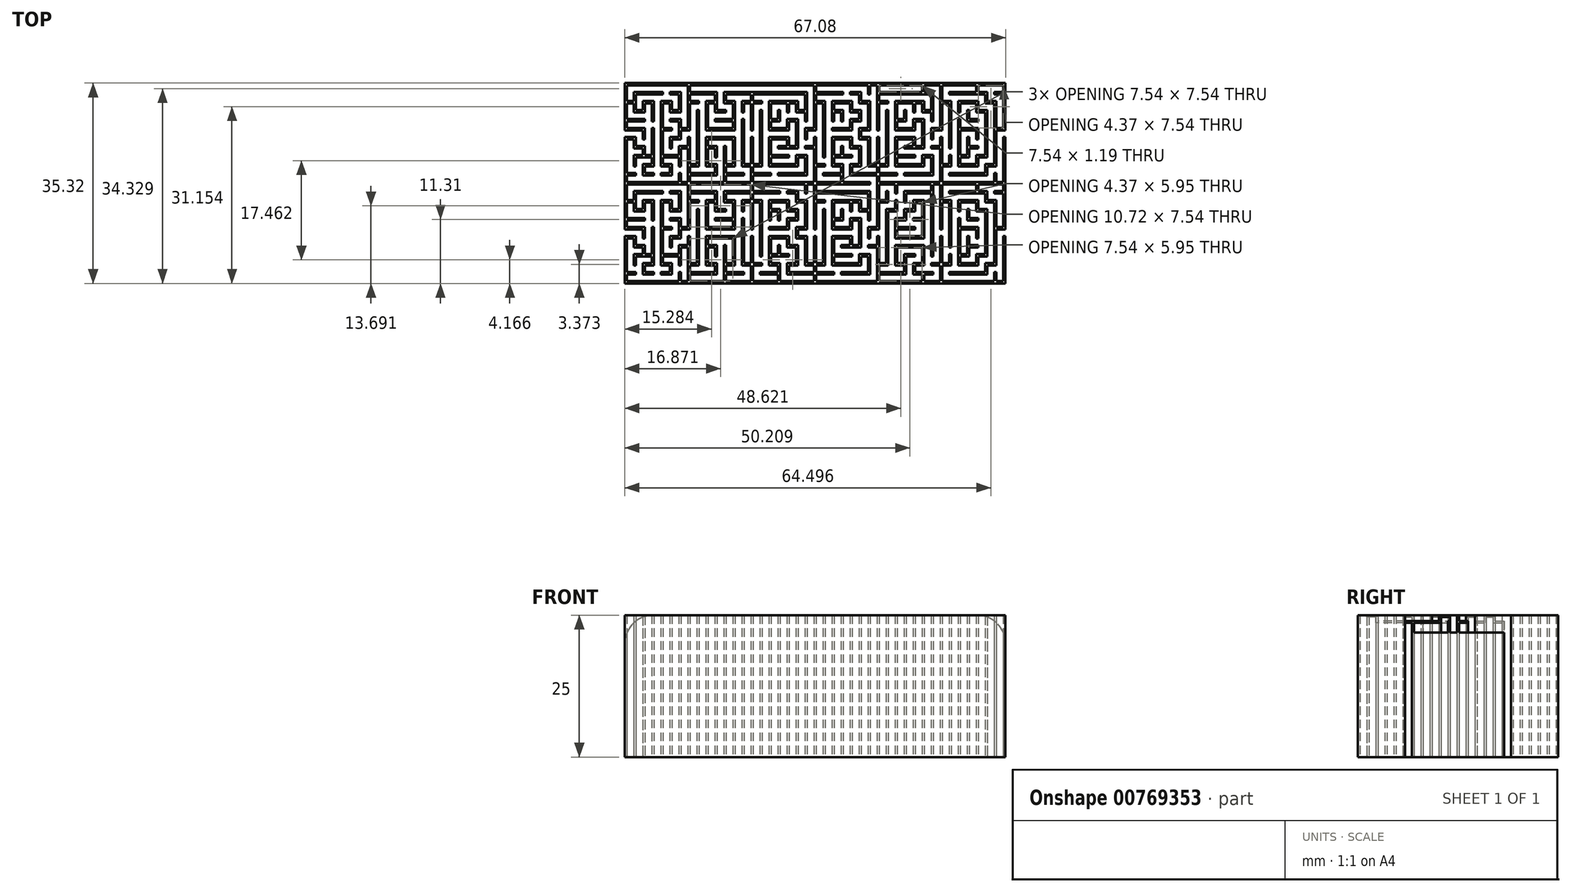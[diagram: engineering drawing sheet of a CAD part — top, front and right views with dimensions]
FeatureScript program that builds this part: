
annotation { "Feature Type Name" : "Feature", "Feature Type Description" : "" }
export const myFeature = defineFeature(function(context is Context, id is Id, definition is map)
    precondition{}
    {
        {
            var Q0;
            Q0=qCreatedBy(makeId("Top.planeOp"),FACE);
            var sketch = newSketch(context, id + "F0", { "sketchPlane" : qUnion([Q0])});
            skLineSegment(sketch, "E0", {"start": v(-25.6, 6.15) * mm, "end": v(-25.6, 8.14) * mm});
            skLineSegment(sketch, "E1", {"start": v(-25.6, 8.14) * mm, "end": v(-24.01, 8.14) * mm});
            skLineSegment(sketch, "E2", {"start": v(-24.01, 8.14) * mm, "end": v(-24.01, 10.91) * mm});
            skLineSegment(sketch, "E3", {"start": v(-24.01, 10.91) * mm, "end": v(-25.6, 10.91) * mm});
            skLineSegment(sketch, "E4", {"start": v(-25.6, 10.91) * mm, "end": v(-25.6, 11.31) * mm});
            skLineSegment(sketch, "E5", {"start": v(-25.6, 11.31) * mm, "end": v(-23.61, 11.31) * mm});
            skLineSegment(sketch, "E6", {"start": v(-23.61, 11.31) * mm, "end": v(-23.61, 9.72) * mm});
            skLineSegment(sketch, "E7", {"start": v(-23.61, 9.72) * mm, "end": v(-22.42, 9.72) * mm});
            skLineSegment(sketch, "E8", {"start": v(-22.42, 9.72) * mm, "end": v(-22.42, 17.26) * mm});
            skLineSegment(sketch, "E9", {"start": v(-22.42, 17.26) * mm, "end": v(-33.14, 17.26) * mm});
            skLineSegment(sketch, "E10", {"start": v(-33.14, 17.26) * mm, "end": v(-33.14, 14.49) * mm});
            skLineSegment(sketch, "E11", {"start": v(-33.14, 14.49) * mm, "end": v(-31.95, 14.49) * mm});
            skLineSegment(sketch, "E12", {"start": v(-31.95, 14.49) * mm, "end": v(-31.95, 16.07) * mm});
            skLineSegment(sketch, "E13", {"start": v(-31.95, 16.07) * mm, "end": v(-26.79, 16.07) * mm});
            skLineSegment(sketch, "E14", {"start": v(-26.79, 16.07) * mm, "end": v(-26.79, 15.68) * mm});
            skLineSegment(sketch, "E15", {"start": v(-26.79, 15.68) * mm, "end": v(-31.55, 15.68) * mm});
            skLineSegment(sketch, "E16", {"start": v(-31.55, 15.68) * mm, "end": v(-31.55, 12.9) * mm});
            skLineSegment(sketch, "E17", {"start": v(-31.55, 12.9) * mm, "end": v(-30.36, 12.9) * mm});
            skLineSegment(sketch, "E18", {"start": v(-30.36, 12.9) * mm, "end": v(-30.36, 14.49) * mm});
            skLineSegment(sketch, "E19", {"start": v(-30.36, 14.49) * mm, "end": v(-28.38, 14.49) * mm});
            skLineSegment(sketch, "E20", {"start": v(-28.38, 14.49) * mm, "end": v(-28.38, 10.91) * mm});
            skLineSegment(sketch, "E21", {"start": v(-28.38, 10.91) * mm, "end": v(-28.77, 10.91) * mm});
            skLineSegment(sketch, "E22", {"start": v(-28.77, 10.91) * mm, "end": v(-28.77, 14.09) * mm});
            skLineSegment(sketch, "E23", {"start": v(-28.77, 14.09) * mm, "end": v(-29.96, 14.09) * mm});
            skLineSegment(sketch, "E24", {"start": v(-29.96, 14.09) * mm, "end": v(-29.96, 12.5) * mm});
            skLineSegment(sketch, "E25", {"start": v(-29.96, 12.5) * mm, "end": v(-31.95, 12.5) * mm});
            skLineSegment(sketch, "E26", {"start": v(-31.95, 12.5) * mm, "end": v(-31.95, 14.09) * mm});
            skLineSegment(sketch, "E27", {"start": v(-31.95, 14.09) * mm, "end": v(-33.14, 14.09) * mm});
            skLineSegment(sketch, "E28", {"start": v(-33.14, 14.09) * mm, "end": v(-33.14, 11.31) * mm});
            skLineSegment(sketch, "E29", {"start": v(-33.14, 11.31) * mm, "end": v(-29.96, 11.31) * mm});
            skLineSegment(sketch, "E30", {"start": v(-29.96, 11.31) * mm, "end": v(-29.96, 10.91) * mm});
            skLineSegment(sketch, "E31", {"start": v(-29.96, 10.91) * mm, "end": v(-33.14, 10.91) * mm});
            skLineSegment(sketch, "E32", {"start": v(-33.14, 10.91) * mm, "end": v(-33.14, 9.72) * mm});
            skLineSegment(sketch, "E33", {"start": v(-33.14, 9.72) * mm, "end": v(-29.96, 9.72) * mm});
            skLineSegment(sketch, "E34", {"start": v(-29.96, 9.72) * mm, "end": v(-29.96, 7.74) * mm});
            skLineSegment(sketch, "E35", {"start": v(-29.96, 7.74) * mm, "end": v(-30.36, 7.74) * mm});
            skLineSegment(sketch, "E36", {"start": v(-30.36, 7.74) * mm, "end": v(-30.36, 9.33) * mm});
            skLineSegment(sketch, "E37", {"start": v(-30.36, 9.33) * mm, "end": v(-33.54, 9.33) * mm});
            skLineSegment(sketch, "E38", {"start": v(-33.54, 9.33) * mm, "end": v(-33.54, 17.66) * mm});
            skLineSegment(sketch, "E39", {"start": v(-33.54, 17.66) * mm, "end": v(-22.03, 17.66) * mm});
            skLineSegment(sketch, "E40", {"start": v(-22.03, 17.66) * mm, "end": v(-22.03, 9.33) * mm});
            skLineSegment(sketch, "E41", {"start": v(-22.03, 9.33) * mm, "end": v(-23.61, 9.33) * mm});
            skLineSegment(sketch, "E42", {"start": v(-23.61, 9.33) * mm, "end": v(-23.61, 7.74) * mm});
            skLineSegment(sketch, "E43", {"start": v(-23.61, 7.74) * mm, "end": v(-25.2, 7.74) * mm});
            skLineSegment(sketch, "E44", {"start": v(-25.2, 7.74) * mm, "end": v(-25.2, 6.15) * mm});
            skLineSegment(sketch, "E45", {"start": v(-25.2, 6.15) * mm, "end": v(-25.6, 6.15) * mm});
            skLineSegment(sketch, "E46", {"start": v(-33.54, -0.2) * mm, "end": v(-33.54, 8.14) * mm});
            skLineSegment(sketch, "E47", {"start": v(-33.54, 8.14) * mm, "end": v(-31.55, 8.14) * mm});
            skLineSegment(sketch, "E48", {"start": v(-31.55, 8.14) * mm, "end": v(-31.55, 6.55) * mm});
            skLineSegment(sketch, "E49", {"start": v(-31.55, 6.55) * mm, "end": v(-29.96, 6.55) * mm});
            skLineSegment(sketch, "E50", {"start": v(-29.96, 6.55) * mm, "end": v(-29.96, 4.96) * mm});
            skLineSegment(sketch, "E51", {"start": v(-29.96, 4.96) * mm, "end": v(-28.77, 4.96) * mm});
            skLineSegment(sketch, "E52", {"start": v(-28.77, 4.96) * mm, "end": v(-28.77, 9.72) * mm});
            skLineSegment(sketch, "E53", {"start": v(-28.77, 9.72) * mm, "end": v(-28.38, 9.72) * mm});
            skLineSegment(sketch, "E54", {"start": v(-28.38, 9.72) * mm, "end": v(-28.38, 2.98) * mm});
            skLineSegment(sketch, "E55", {"start": v(-28.38, 2.98) * mm, "end": v(-29.96, 2.98) * mm});
            skLineSegment(sketch, "E56", {"start": v(-29.96, 2.98) * mm, "end": v(-29.96, 1.79) * mm});
            skLineSegment(sketch, "E57", {"start": v(-29.96, 1.79) * mm, "end": v(-28.38, 1.79) * mm});
            skLineSegment(sketch, "E58", {"start": v(-28.38, 1.79) * mm, "end": v(-28.38, 1.39) * mm});
            skLineSegment(sketch, "E59", {"start": v(-28.38, 1.39) * mm, "end": v(-30.36, 1.39) * mm});
            skLineSegment(sketch, "E60", {"start": v(-30.36, 1.39) * mm, "end": v(-30.36, 3.37) * mm});
            skLineSegment(sketch, "E61", {"start": v(-30.36, 3.37) * mm, "end": v(-28.77, 3.37) * mm});
            skLineSegment(sketch, "E62", {"start": v(-28.77, 3.37) * mm, "end": v(-28.77, 4.56) * mm});
            skLineSegment(sketch, "E63", {"start": v(-28.77, 4.56) * mm, "end": v(-31.55, 4.56) * mm});
            skLineSegment(sketch, "E64", {"start": v(-31.55, 4.56) * mm, "end": v(-31.55, 2.98) * mm});
            skLineSegment(sketch, "E65", {"start": v(-31.55, 2.98) * mm, "end": v(-31.95, 2.98) * mm});
            skLineSegment(sketch, "E66", {"start": v(-31.95, 2.98) * mm, "end": v(-31.95, 4.96) * mm});
            skLineSegment(sketch, "E67", {"start": v(-31.95, 4.96) * mm, "end": v(-30.36, 4.96) * mm});
            skLineSegment(sketch, "E68", {"start": v(-30.36, 4.96) * mm, "end": v(-30.36, 6.15) * mm});
            skLineSegment(sketch, "E69", {"start": v(-30.36, 6.15) * mm, "end": v(-31.95, 6.15) * mm});
            skLineSegment(sketch, "E70", {"start": v(-31.95, 6.15) * mm, "end": v(-31.95, 7.74) * mm});
            skLineSegment(sketch, "E71", {"start": v(-31.95, 7.74) * mm, "end": v(-33.14, 7.74) * mm});
            skLineSegment(sketch, "E72", {"start": v(-33.14, 7.74) * mm, "end": v(-33.14, 1.79) * mm});
            skLineSegment(sketch, "E73", {"start": v(-33.14, 1.79) * mm, "end": v(-31.55, 1.79) * mm});
            skLineSegment(sketch, "E74", {"start": v(-31.55, 1.79) * mm, "end": v(-31.55, 1.39) * mm});
            skLineSegment(sketch, "E75", {"start": v(-31.55, 1.39) * mm, "end": v(-33.14, 1.39) * mm});
            skLineSegment(sketch, "E76", {"start": v(-33.14, 1.39) * mm, "end": v(-33.14, 0.2) * mm});
            skLineSegment(sketch, "E77", {"start": v(-33.14, 0.2) * mm, "end": v(-24.01, 0.2) * mm});
            skLineSegment(sketch, "E78", {"start": v(-24.01, 0.2) * mm, "end": v(-24.01, 1.79) * mm});
            skLineSegment(sketch, "E79", {"start": v(-24.01, 1.79) * mm, "end": v(-23.61, 1.79) * mm});
            skLineSegment(sketch, "E80", {"start": v(-23.61, 1.79) * mm, "end": v(-23.61, 0.2) * mm});
            skLineSegment(sketch, "E81", {"start": v(-23.61, 0.2) * mm, "end": v(-22.42, 0.2) * mm});
            skLineSegment(sketch, "E82", {"start": v(-22.42, 0.2) * mm, "end": v(-22.42, 6.15) * mm});
            skLineSegment(sketch, "E83", {"start": v(-22.42, 6.15) * mm, "end": v(-23.61, 6.15) * mm});
            skLineSegment(sketch, "E84", {"start": v(-23.61, 6.15) * mm, "end": v(-23.61, 2.98) * mm});
            skLineSegment(sketch, "E85", {"start": v(-23.61, 2.98) * mm, "end": v(-24.01, 2.98) * mm});
            skLineSegment(sketch, "E86", {"start": v(-24.01, 2.98) * mm, "end": v(-24.01, 4.56) * mm});
            skLineSegment(sketch, "E87", {"start": v(-24.01, 4.56) * mm, "end": v(-26.79, 4.56) * mm});
            skLineSegment(sketch, "E88", {"start": v(-26.79, 4.56) * mm, "end": v(-26.79, 3.37) * mm});
            skLineSegment(sketch, "E89", {"start": v(-26.79, 3.37) * mm, "end": v(-25.2, 3.37) * mm});
            skLineSegment(sketch, "E90", {"start": v(-25.2, 3.37) * mm, "end": v(-25.2, 1.39) * mm});
            skLineSegment(sketch, "E91", {"start": v(-25.2, 1.39) * mm, "end": v(-27.19, 1.39) * mm});
            skLineSegment(sketch, "E92", {"start": v(-27.19, 1.39) * mm, "end": v(-27.19, 1.79) * mm});
            skLineSegment(sketch, "E93", {"start": v(-27.19, 1.79) * mm, "end": v(-25.6, 1.79) * mm});
            skLineSegment(sketch, "E94", {"start": v(-25.6, 1.79) * mm, "end": v(-25.6, 2.98) * mm});
            skLineSegment(sketch, "E95", {"start": v(-25.6, 2.98) * mm, "end": v(-27.19, 2.98) * mm});
            skLineSegment(sketch, "E96", {"start": v(-27.19, 2.98) * mm, "end": v(-27.19, 14.49) * mm});
            skLineSegment(sketch, "E97", {"start": v(-27.19, 14.49) * mm, "end": v(-25.2, 14.49) * mm});
            skLineSegment(sketch, "E98", {"start": v(-25.2, 14.49) * mm, "end": v(-25.2, 12.9) * mm});
            skLineSegment(sketch, "E99", {"start": v(-25.2, 12.9) * mm, "end": v(-24.01, 12.9) * mm});
            skLineSegment(sketch, "E100", {"start": v(-24.01, 12.9) * mm, "end": v(-24.01, 15.68) * mm});
            skLineSegment(sketch, "E101", {"start": v(-24.01, 15.68) * mm, "end": v(-25.6, 15.68) * mm});
            skLineSegment(sketch, "E102", {"start": v(-25.6, 15.68) * mm, "end": v(-25.6, 16.07) * mm});
            skLineSegment(sketch, "E103", {"start": v(-25.6, 16.07) * mm, "end": v(-23.61, 16.07) * mm});
            skLineSegment(sketch, "E104", {"start": v(-23.61, 16.07) * mm, "end": v(-23.61, 12.5) * mm});
            skLineSegment(sketch, "E105", {"start": v(-23.61, 12.5) * mm, "end": v(-25.6, 12.5) * mm});
            skLineSegment(sketch, "E106", {"start": v(-25.6, 12.5) * mm, "end": v(-25.6, 14.09) * mm});
            skLineSegment(sketch, "E107", {"start": v(-25.6, 14.09) * mm, "end": v(-26.79, 14.09) * mm});
            skLineSegment(sketch, "E108", {"start": v(-26.79, 14.09) * mm, "end": v(-26.79, 9.72) * mm});
            skLineSegment(sketch, "E109", {"start": v(-26.79, 9.72) * mm, "end": v(-25.2, 9.72) * mm});
            skLineSegment(sketch, "E110", {"start": v(-25.2, 9.72) * mm, "end": v(-25.2, 9.33) * mm});
            skLineSegment(sketch, "E111", {"start": v(-25.2, 9.33) * mm, "end": v(-26.79, 9.33) * mm});
            skLineSegment(sketch, "E112", {"start": v(-26.79, 9.33) * mm, "end": v(-26.79, 4.96) * mm});
            skLineSegment(sketch, "E113", {"start": v(-26.79, 4.96) * mm, "end": v(-24.01, 4.96) * mm});
            skLineSegment(sketch, "E114", {"start": v(-24.01, 4.96) * mm, "end": v(-24.01, 6.55) * mm});
            skLineSegment(sketch, "E115", {"start": v(-24.01, 6.55) * mm, "end": v(-22.42, 6.55) * mm});
            skLineSegment(sketch, "E116", {"start": v(-22.42, 6.55) * mm, "end": v(-22.42, 8.14) * mm});
            skLineSegment(sketch, "E117", {"start": v(-22.42, 8.14) * mm, "end": v(-22.03, 8.14) * mm});
            skLineSegment(sketch, "E118", {"start": v(-22.03, 8.14) * mm, "end": v(-22.03, -0.2) * mm});
            skLineSegment(sketch, "E119", {"start": v(-22.03, -0.2) * mm, "end": v(-33.54, -0.2) * mm});
            skLineSegment(sketch, "E120", {"start": v(-22.42, 9.33) * mm, "end": v(-22.42, 17.66) * mm});
            skLineSegment(sketch, "E121", {"start": v(-22.42, 17.66) * mm, "end": v(-10.91, 17.66) * mm});
            skLineSegment(sketch, "E122", {"start": v(-10.91, 9.33) * mm, "end": v(-11.31, 9.33) * mm});
            skLineSegment(sketch, "E123", {"start": v(-11.31, 9.33) * mm, "end": v(-11.31, 14.09) * mm});
            skLineSegment(sketch, "E124", {"start": v(-11.31, 14.09) * mm, "end": v(-12.5, 14.09) * mm});
            skLineSegment(sketch, "E125", {"start": v(-12.5, 14.09) * mm, "end": v(-12.5, 12.5) * mm});
            skLineSegment(sketch, "E126", {"start": v(-12.5, 12.5) * mm, "end": v(-12.9, 12.5) * mm});
            skLineSegment(sketch, "E127", {"start": v(-12.9, 12.5) * mm, "end": v(-12.9, 14.49) * mm});
            skLineSegment(sketch, "E128", {"start": v(-12.9, 14.49) * mm, "end": v(-11.31, 14.49) * mm});
            skLineSegment(sketch, "E129", {"start": v(-11.31, 14.49) * mm, "end": v(-11.31, 15.68) * mm});
            skLineSegment(sketch, "E130", {"start": v(-11.31, 15.68) * mm, "end": v(-15.68, 15.68) * mm});
            skLineSegment(sketch, "E131", {"start": v(-15.68, 15.68) * mm, "end": v(-15.68, 14.49) * mm});
            skLineSegment(sketch, "E132", {"start": v(-15.68, 14.49) * mm, "end": v(-14.09, 14.49) * mm});
            skLineSegment(sketch, "E133", {"start": v(-14.09, 14.49) * mm, "end": v(-14.09, 9.33) * mm});
            skLineSegment(sketch, "E134", {"start": v(-14.09, 9.33) * mm, "end": v(-19.25, 9.33) * mm});
            skLineSegment(sketch, "E135", {"start": v(-19.25, 9.33) * mm, "end": v(-19.25, 14.49) * mm});
            skLineSegment(sketch, "E136", {"start": v(-19.25, 14.49) * mm, "end": v(-17.66, 14.49) * mm});
            skLineSegment(sketch, "E137", {"start": v(-17.66, 14.49) * mm, "end": v(-17.66, 15.68) * mm});
            skLineSegment(sketch, "E138", {"start": v(-17.66, 15.68) * mm, "end": v(-22.03, 15.68) * mm});
            skLineSegment(sketch, "E139", {"start": v(-22.03, 15.68) * mm, "end": v(-22.03, 14.49) * mm});
            skLineSegment(sketch, "E140", {"start": v(-22.03, 14.49) * mm, "end": v(-20.44, 14.49) * mm});
            skLineSegment(sketch, "E141", {"start": v(-20.44, 14.49) * mm, "end": v(-20.44, 14.09) * mm});
            skLineSegment(sketch, "E142", {"start": v(-20.44, 14.09) * mm, "end": v(-22.03, 14.09) * mm});
            skLineSegment(sketch, "E143", {"start": v(-22.03, 14.09) * mm, "end": v(-22.03, 9.33) * mm});
            skLineSegment(sketch, "E144", {"start": v(-22.03, 9.33) * mm, "end": v(-22.42, 9.33) * mm});
            skLineSegment(sketch, "E145", {"start": v(-22.42, -0.2) * mm, "end": v(-22.42, 8.14) * mm});
            skLineSegment(sketch, "E146", {"start": v(-22.03, 8.14) * mm, "end": v(-22.03, 3.37) * mm});
            skLineSegment(sketch, "E147", {"start": v(-22.03, 3.37) * mm, "end": v(-20.84, 3.37) * mm});
            skLineSegment(sketch, "E148", {"start": v(-20.84, 3.37) * mm, "end": v(-20.84, 12.9) * mm});
            skLineSegment(sketch, "E149", {"start": v(-20.84, 12.9) * mm, "end": v(-20.44, 12.9) * mm});
            skLineSegment(sketch, "E150", {"start": v(-20.44, 12.9) * mm, "end": v(-20.44, 2.98) * mm});
            skLineSegment(sketch, "E151", {"start": v(-20.44, 2.98) * mm, "end": v(-22.03, 2.98) * mm});
            skLineSegment(sketch, "E152", {"start": v(-22.03, 2.98) * mm, "end": v(-22.03, 1.79) * mm});
            skLineSegment(sketch, "E153", {"start": v(-22.03, 1.79) * mm, "end": v(-17.66, 1.79) * mm});
            skLineSegment(sketch, "E154", {"start": v(-17.66, 1.79) * mm, "end": v(-17.66, 2.98) * mm});
            skLineSegment(sketch, "E155", {"start": v(-17.66, 2.98) * mm, "end": v(-19.25, 2.98) * mm});
            skLineSegment(sketch, "E156", {"start": v(-19.25, 2.98) * mm, "end": v(-19.25, 8.14) * mm});
            skLineSegment(sketch, "E157", {"start": v(-19.25, 8.14) * mm, "end": v(-14.09, 8.14) * mm});
            skLineSegment(sketch, "E158", {"start": v(-14.09, 8.14) * mm, "end": v(-14.09, 2.98) * mm});
            skLineSegment(sketch, "E159", {"start": v(-14.09, 2.98) * mm, "end": v(-15.68, 2.98) * mm});
            skLineSegment(sketch, "E160", {"start": v(-15.68, 2.98) * mm, "end": v(-15.68, 1.79) * mm});
            skLineSegment(sketch, "E161", {"start": v(-15.68, 1.79) * mm, "end": v(-12.5, 1.79) * mm});
            skLineSegment(sketch, "E162", {"start": v(-12.5, 1.79) * mm, "end": v(-12.5, 1.39) * mm});
            skLineSegment(sketch, "E163", {"start": v(-12.5, 1.39) * mm, "end": v(-15.68, 1.39) * mm});
            skLineSegment(sketch, "E164", {"start": v(-15.68, 1.39) * mm, "end": v(-15.68, 0.2) * mm});
            skLineSegment(sketch, "E165", {"start": v(-15.68, 0.2) * mm, "end": v(-11.31, 0.2) * mm});
            skLineSegment(sketch, "E166", {"start": v(-11.31, 0.2) * mm, "end": v(-11.31, 2.98) * mm});
            skLineSegment(sketch, "E167", {"start": v(-11.31, 2.98) * mm, "end": v(-12.9, 2.98) * mm});
            skLineSegment(sketch, "E168", {"start": v(-12.9, 2.98) * mm, "end": v(-12.9, 11.31) * mm});
            skLineSegment(sketch, "E169", {"start": v(-12.9, 11.31) * mm, "end": v(-12.5, 11.31) * mm});
            skLineSegment(sketch, "E170", {"start": v(-12.5, 11.31) * mm, "end": v(-12.5, 3.37) * mm});
            skLineSegment(sketch, "E171", {"start": v(-12.5, 3.37) * mm, "end": v(-11.31, 3.37) * mm});
            skLineSegment(sketch, "E172", {"start": v(-11.31, 3.37) * mm, "end": v(-11.31, 8.14) * mm});
            skLineSegment(sketch, "E173", {"start": v(-11.31, 8.14) * mm, "end": v(-10.91, 8.14) * mm});
            skLineSegment(sketch, "E174", {"start": v(-10.91, 8.14) * mm, "end": v(-10.91, -0.2) * mm});
            skLineSegment(sketch, "E175", {"start": v(-10.91, -0.2) * mm, "end": v(-22.42, -0.2) * mm});
            skLineSegment(sketch, "E176", {"start": v(-14.49, 9.72) * mm, "end": v(-14.49, 10.91) * mm});
            skLineSegment(sketch, "E177", {"start": v(-14.49, 10.91) * mm, "end": v(-17.66, 10.91) * mm});
            skLineSegment(sketch, "E178", {"start": v(-17.66, 10.91) * mm, "end": v(-17.66, 11.31) * mm});
            skLineSegment(sketch, "E179", {"start": v(-17.66, 11.31) * mm, "end": v(-14.49, 11.31) * mm});
            skLineSegment(sketch, "E180", {"start": v(-14.49, 11.31) * mm, "end": v(-14.49, 14.09) * mm});
            skLineSegment(sketch, "E181", {"start": v(-14.49, 14.09) * mm, "end": v(-16.07, 14.09) * mm});
            skLineSegment(sketch, "E182", {"start": v(-16.07, 14.09) * mm, "end": v(-16.07, 16.07) * mm});
            skLineSegment(sketch, "E183", {"start": v(-16.07, 16.07) * mm, "end": v(-11.31, 16.07) * mm});
            skLineSegment(sketch, "E184", {"start": v(-11.31, 17.26) * mm, "end": v(-22.03, 17.26) * mm});
            skLineSegment(sketch, "E185", {"start": v(-22.03, 17.26) * mm, "end": v(-22.03, 16.07) * mm});
            skLineSegment(sketch, "E186", {"start": v(-22.03, 16.07) * mm, "end": v(-17.26, 16.07) * mm});
            skLineSegment(sketch, "E187", {"start": v(-17.26, 16.07) * mm, "end": v(-17.26, 12.9) * mm});
            skLineSegment(sketch, "E188", {"start": v(-17.26, 12.9) * mm, "end": v(-15.68, 12.9) * mm});
            skLineSegment(sketch, "E189", {"start": v(-15.68, 12.9) * mm, "end": v(-15.68, 12.5) * mm});
            skLineSegment(sketch, "E190", {"start": v(-15.68, 12.5) * mm, "end": v(-17.66, 12.5) * mm});
            skLineSegment(sketch, "E191", {"start": v(-17.66, 12.5) * mm, "end": v(-17.66, 14.09) * mm});
            skLineSegment(sketch, "E192", {"start": v(-17.66, 14.09) * mm, "end": v(-18.85, 14.09) * mm});
            skLineSegment(sketch, "E193", {"start": v(-18.85, 14.09) * mm, "end": v(-18.85, 9.72) * mm});
            skLineSegment(sketch, "E194", {"start": v(-18.85, 9.72) * mm, "end": v(-14.49, 9.72) * mm});
            skLineSegment(sketch, "E195", {"start": v(-16.07, 0.2) * mm, "end": v(-16.07, 6.55) * mm});
            skLineSegment(sketch, "E196", {"start": v(-16.07, 6.55) * mm, "end": v(-15.68, 6.55) * mm});
            skLineSegment(sketch, "E197", {"start": v(-15.68, 6.55) * mm, "end": v(-15.68, 3.37) * mm});
            skLineSegment(sketch, "E198", {"start": v(-15.68, 3.37) * mm, "end": v(-14.49, 3.37) * mm});
            skLineSegment(sketch, "E199", {"start": v(-14.49, 3.37) * mm, "end": v(-14.49, 7.74) * mm});
            skLineSegment(sketch, "E200", {"start": v(-14.49, 7.74) * mm, "end": v(-18.85, 7.74) * mm});
            skLineSegment(sketch, "E201", {"start": v(-18.85, 7.74) * mm, "end": v(-18.85, 6.55) * mm});
            skLineSegment(sketch, "E202", {"start": v(-18.85, 6.55) * mm, "end": v(-17.26, 6.55) * mm});
            skLineSegment(sketch, "E203", {"start": v(-17.26, 6.55) * mm, "end": v(-17.26, 4.56) * mm});
            skLineSegment(sketch, "E204", {"start": v(-17.26, 4.56) * mm, "end": v(-17.66, 4.56) * mm});
            skLineSegment(sketch, "E205", {"start": v(-17.66, 4.56) * mm, "end": v(-17.66, 6.15) * mm});
            skLineSegment(sketch, "E206", {"start": v(-17.66, 6.15) * mm, "end": v(-18.85, 6.15) * mm});
            skLineSegment(sketch, "E207", {"start": v(-18.85, 6.15) * mm, "end": v(-18.85, 3.37) * mm});
            skLineSegment(sketch, "E208", {"start": v(-18.85, 3.37) * mm, "end": v(-17.26, 3.37) * mm});
            skLineSegment(sketch, "E209", {"start": v(-17.26, 3.37) * mm, "end": v(-17.26, 1.39) * mm});
            skLineSegment(sketch, "E210", {"start": v(-17.26, 1.39) * mm, "end": v(-22.03, 1.39) * mm});
            skLineSegment(sketch, "E211", {"start": v(-22.03, 1.39) * mm, "end": v(-22.03, 0.2) * mm});
            skLineSegment(sketch, "E212", {"start": v(-22.03, 0.2) * mm, "end": v(-16.07, 0.2) * mm});
            skLineSegment(sketch, "E213", {"start": v(-6.55, 1.39) * mm, "end": v(-6.55, 1.79) * mm});
            skLineSegment(sketch, "E214", {"start": v(-6.55, 1.79) * mm, "end": v(-1.79, 1.79) * mm});
            skLineSegment(sketch, "E215", {"start": v(-1.79, 1.79) * mm, "end": v(-1.79, 4.56) * mm});
            skLineSegment(sketch, "E216", {"start": v(-1.79, 4.56) * mm, "end": v(-2.98, 4.56) * mm});
            skLineSegment(sketch, "E217", {"start": v(-2.98, 4.56) * mm, "end": v(-2.98, 2.98) * mm});
            skLineSegment(sketch, "E218", {"start": v(-2.98, 2.98) * mm, "end": v(-8.14, 2.98) * mm});
            skLineSegment(sketch, "E219", {"start": v(-8.14, 2.98) * mm, "end": v(-8.14, 8.14) * mm});
            skLineSegment(sketch, "E220", {"start": v(-8.14, 8.14) * mm, "end": v(-4.56, 8.14) * mm});
            skLineSegment(sketch, "E221", {"start": v(-4.56, 8.14) * mm, "end": v(-4.56, 6.55) * mm});
            skLineSegment(sketch, "E222", {"start": v(-4.56, 6.55) * mm, "end": v(-3.37, 6.55) * mm});
            skLineSegment(sketch, "E223", {"start": v(-3.37, 6.55) * mm, "end": v(-3.37, 10.91) * mm});
            skLineSegment(sketch, "E224", {"start": v(-3.37, 10.91) * mm, "end": v(-4.56, 10.91) * mm});
            skLineSegment(sketch, "E225", {"start": v(-4.56, 10.91) * mm, "end": v(-4.56, 9.33) * mm});
            skLineSegment(sketch, "E226", {"start": v(-4.56, 9.33) * mm, "end": v(-8.14, 9.33) * mm});
            skLineSegment(sketch, "E227", {"start": v(-8.14, 9.33) * mm, "end": v(-8.14, 14.49) * mm});
            skLineSegment(sketch, "E228", {"start": v(-8.14, 14.49) * mm, "end": v(-2.98, 14.49) * mm});
            skLineSegment(sketch, "E229", {"start": v(-2.98, 14.49) * mm, "end": v(-2.98, 12.9) * mm});
            skLineSegment(sketch, "E230", {"start": v(-2.98, 12.9) * mm, "end": v(-1.79, 12.9) * mm});
            skLineSegment(sketch, "E231", {"start": v(-1.79, 12.9) * mm, "end": v(-1.79, 15.68) * mm});
            skLineSegment(sketch, "E232", {"start": v(-1.79, 15.68) * mm, "end": v(-10.91, 15.68) * mm});
            skLineSegment(sketch, "E233", {"start": v(-10.91, 15.68) * mm, "end": v(-10.91, 14.49) * mm});
            skLineSegment(sketch, "E234", {"start": v(-10.91, 14.49) * mm, "end": v(-9.33, 14.49) * mm});
            skLineSegment(sketch, "E235", {"start": v(-9.33, 14.49) * mm, "end": v(-9.33, 14.09) * mm});
            skLineSegment(sketch, "E236", {"start": v(-9.33, 14.09) * mm, "end": v(-10.91, 14.09) * mm});
            skLineSegment(sketch, "E237", {"start": v(-10.91, 14.09) * mm, "end": v(-10.91, 9.33) * mm});
            skLineSegment(sketch, "E238", {"start": v(-11.31, 17.66) * mm, "end": v(0.2, 17.66) * mm});
            skLineSegment(sketch, "E239", {"start": v(0.2, 17.26) * mm, "end": v(0.2, 9.33) * mm});
            skLineSegment(sketch, "E240", {"start": v(0.2, 9.33) * mm, "end": v(-1.39, 9.33) * mm});
            skLineSegment(sketch, "E241", {"start": v(-1.39, 9.33) * mm, "end": v(-1.39, 7.74) * mm});
            skLineSegment(sketch, "E242", {"start": v(-1.39, 7.74) * mm, "end": v(-1.79, 7.74) * mm});
            skLineSegment(sketch, "E243", {"start": v(-1.79, 7.74) * mm, "end": v(-1.79, 9.72) * mm});
            skLineSegment(sketch, "E244", {"start": v(-1.79, 9.72) * mm, "end": v(-0.2, 9.72) * mm});
            skLineSegment(sketch, "E245", {"start": v(-0.2, 9.72) * mm, "end": v(-0.2, 17.26) * mm});
            skLineSegment(sketch, "E246", {"start": v(-0.2, 17.26) * mm, "end": v(-2.98, 17.26) * mm});
            skLineSegment(sketch, "E247", {"start": v(-2.98, 16.07) * mm, "end": v(-1.39, 16.07) * mm});
            skLineSegment(sketch, "E248", {"start": v(-1.39, 16.07) * mm, "end": v(-1.39, 10.91) * mm});
            skLineSegment(sketch, "E249", {"start": v(-1.39, 10.91) * mm, "end": v(-1.79, 10.91) * mm});
            skLineSegment(sketch, "E250", {"start": v(-1.79, 10.91) * mm, "end": v(-1.79, 12.5) * mm});
            skLineSegment(sketch, "E251", {"start": v(-1.79, 12.5) * mm, "end": v(-3.37, 12.5) * mm});
            skLineSegment(sketch, "E252", {"start": v(-3.37, 12.5) * mm, "end": v(-3.37, 14.09) * mm});
            skLineSegment(sketch, "E253", {"start": v(-3.37, 14.09) * mm, "end": v(-4.56, 14.09) * mm});
            skLineSegment(sketch, "E254", {"start": v(-4.56, 14.09) * mm, "end": v(-4.56, 12.5) * mm});
            skLineSegment(sketch, "E255", {"start": v(-4.56, 12.5) * mm, "end": v(-4.96, 12.5) * mm});
            skLineSegment(sketch, "E256", {"start": v(-4.96, 12.5) * mm, "end": v(-4.96, 14.09) * mm});
            skLineSegment(sketch, "E257", {"start": v(-4.96, 14.09) * mm, "end": v(-7.74, 14.09) * mm});
            skLineSegment(sketch, "E258", {"start": v(-7.74, 14.09) * mm, "end": v(-7.74, 11.31) * mm});
            skLineSegment(sketch, "E259", {"start": v(-7.74, 11.31) * mm, "end": v(-6.55, 11.31) * mm});
            skLineSegment(sketch, "E260", {"start": v(-6.55, 11.31) * mm, "end": v(-6.55, 12.9) * mm});
            skLineSegment(sketch, "E261", {"start": v(-6.55, 12.9) * mm, "end": v(-6.15, 12.9) * mm});
            skLineSegment(sketch, "E262", {"start": v(-6.15, 12.9) * mm, "end": v(-6.15, 10.91) * mm});
            skLineSegment(sketch, "E263", {"start": v(-6.15, 10.91) * mm, "end": v(-7.74, 10.91) * mm});
            skLineSegment(sketch, "E264", {"start": v(-7.74, 10.91) * mm, "end": v(-7.74, 9.72) * mm});
            skLineSegment(sketch, "E265", {"start": v(-7.74, 9.72) * mm, "end": v(-4.96, 9.72) * mm});
            skLineSegment(sketch, "E266", {"start": v(-4.96, 9.72) * mm, "end": v(-4.96, 11.31) * mm});
            skLineSegment(sketch, "E267", {"start": v(-4.96, 11.31) * mm, "end": v(-2.98, 11.31) * mm});
            skLineSegment(sketch, "E268", {"start": v(-2.98, 11.31) * mm, "end": v(-2.98, 6.15) * mm});
            skLineSegment(sketch, "E269", {"start": v(-2.98, 6.15) * mm, "end": v(-6.55, 6.15) * mm});
            skLineSegment(sketch, "E270", {"start": v(-6.55, 6.15) * mm, "end": v(-6.55, 6.55) * mm});
            skLineSegment(sketch, "E271", {"start": v(-6.55, 6.55) * mm, "end": v(-4.96, 6.55) * mm});
            skLineSegment(sketch, "E272", {"start": v(-4.96, 6.55) * mm, "end": v(-4.96, 7.74) * mm});
            skLineSegment(sketch, "E273", {"start": v(-4.96, 7.74) * mm, "end": v(-7.74, 7.74) * mm});
            skLineSegment(sketch, "E274", {"start": v(-7.74, 7.74) * mm, "end": v(-7.74, 4.96) * mm});
            skLineSegment(sketch, "E275", {"start": v(-7.74, 4.96) * mm, "end": v(-4.56, 4.96) * mm});
            skLineSegment(sketch, "E276", {"start": v(-4.56, 4.96) * mm, "end": v(-4.56, 4.56) * mm});
            skLineSegment(sketch, "E277", {"start": v(-4.56, 4.56) * mm, "end": v(-7.74, 4.56) * mm});
            skLineSegment(sketch, "E278", {"start": v(-7.74, 4.56) * mm, "end": v(-7.74, 3.37) * mm});
            skLineSegment(sketch, "E279", {"start": v(-7.74, 3.37) * mm, "end": v(-3.37, 3.37) * mm});
            skLineSegment(sketch, "E280", {"start": v(-3.37, 3.37) * mm, "end": v(-3.37, 4.96) * mm});
            skLineSegment(sketch, "E281", {"start": v(-3.37, 4.96) * mm, "end": v(-1.39, 4.96) * mm});
            skLineSegment(sketch, "E282", {"start": v(-1.39, 4.96) * mm, "end": v(-1.39, 1.39) * mm});
            skLineSegment(sketch, "E283", {"start": v(-1.39, 1.39) * mm, "end": v(-6.55, 1.39) * mm});
            skLineSegment(sketch, "E284", {"start": v(-11.31, -0.2) * mm, "end": v(-11.31, 8.14) * mm});
            skLineSegment(sketch, "E285", {"start": v(-10.91, 8.14) * mm, "end": v(-10.91, 3.37) * mm});
            skLineSegment(sketch, "E286", {"start": v(-10.91, 3.37) * mm, "end": v(-9.72, 3.37) * mm});
            skLineSegment(sketch, "E287", {"start": v(-9.72, 3.37) * mm, "end": v(-9.72, 12.9) * mm});
            skLineSegment(sketch, "E288", {"start": v(-9.72, 12.9) * mm, "end": v(-9.33, 12.9) * mm});
            skLineSegment(sketch, "E289", {"start": v(-9.33, 12.9) * mm, "end": v(-9.33, 2.98) * mm});
            skLineSegment(sketch, "E290", {"start": v(-9.33, 2.98) * mm, "end": v(-10.91, 2.98) * mm});
            skLineSegment(sketch, "E291", {"start": v(-10.91, 2.98) * mm, "end": v(-10.91, 1.79) * mm});
            skLineSegment(sketch, "E292", {"start": v(-10.91, 1.79) * mm, "end": v(-7.74, 1.79) * mm});
            skLineSegment(sketch, "E293", {"start": v(-7.74, 1.79) * mm, "end": v(-7.74, 1.39) * mm});
            skLineSegment(sketch, "E294", {"start": v(-7.74, 1.39) * mm, "end": v(-10.91, 1.39) * mm});
            skLineSegment(sketch, "E295", {"start": v(-10.91, 1.39) * mm, "end": v(-10.91, 0.2) * mm});
            skLineSegment(sketch, "E296", {"start": v(-10.91, 0.2) * mm, "end": v(-0.2, 0.2) * mm});
            skLineSegment(sketch, "E297", {"start": v(-0.2, 0.2) * mm, "end": v(-0.2, 6.15) * mm});
            skLineSegment(sketch, "E298", {"start": v(-0.2, 6.15) * mm, "end": v(-1.79, 6.15) * mm});
            skLineSegment(sketch, "E299", {"start": v(-1.79, 6.15) * mm, "end": v(-1.79, 6.55) * mm});
            skLineSegment(sketch, "E300", {"start": v(-1.79, 6.55) * mm, "end": v(-0.2, 6.55) * mm});
            skLineSegment(sketch, "E301", {"start": v(-0.2, 6.55) * mm, "end": v(-0.2, 8.14) * mm});
            skLineSegment(sketch, "E302", {"start": v(-0.2, 8.14) * mm, "end": v(0.2, 8.14) * mm});
            skLineSegment(sketch, "E303", {"start": v(0.2, 8.14) * mm, "end": v(0.2, -0.2) * mm});
            skLineSegment(sketch, "E304", {"start": v(0.2, -0.2) * mm, "end": v(-11.31, -0.2) * mm});
            skLineSegment(sketch, "E305", {"start": v(-3.37, 17.26) * mm, "end": v(-10.91, 17.26) * mm});
            skLineSegment(sketch, "E306", {"start": v(-10.91, 16.07) * mm, "end": v(-3.37, 16.07) * mm});
            skLineSegment(sketch, "E307", {"start": v(1.39, 4.56) * mm, "end": v(1.39, 14.09) * mm});
            skLineSegment(sketch, "E308", {"start": v(1.39, 14.09) * mm, "end": v(0.2, 14.09) * mm});
            skLineSegment(sketch, "E309", {"start": v(0.2, 14.09) * mm, "end": v(0.2, 9.33) * mm});
            skLineSegment(sketch, "E310", {"start": v(0.2, 9.33) * mm, "end": v(-0.2, 9.33) * mm});
            skLineSegment(sketch, "E311", {"start": v(-0.2, 9.33) * mm, "end": v(-0.2, 17.26) * mm});
            skLineSegment(sketch, "E312", {"start": v(-0.2, 17.66) * mm, "end": v(11.31, 17.66) * mm});
            skLineSegment(sketch, "E313", {"start": v(11.31, 17.66) * mm, "end": v(11.31, 9.33) * mm});
            skLineSegment(sketch, "E314", {"start": v(11.31, 9.33) * mm, "end": v(10.91, 9.33) * mm});
            skLineSegment(sketch, "E315", {"start": v(10.91, 9.33) * mm, "end": v(10.91, 17.26) * mm});
            skLineSegment(sketch, "E316", {"start": v(10.91, 17.26) * mm, "end": v(9.72, 17.26) * mm});
            skLineSegment(sketch, "E317", {"start": v(9.72, 17.26) * mm, "end": v(9.72, 15.68) * mm});
            skLineSegment(sketch, "E318", {"start": v(9.72, 15.68) * mm, "end": v(9.33, 15.68) * mm});
            skLineSegment(sketch, "E319", {"start": v(9.33, 15.68) * mm, "end": v(9.33, 17.26) * mm});
            skLineSegment(sketch, "E320", {"start": v(9.33, 17.26) * mm, "end": v(0.2, 17.26) * mm});
            skLineSegment(sketch, "E321", {"start": v(0.2, 17.26) * mm, "end": v(0.2, 16.07) * mm});
            skLineSegment(sketch, "E322", {"start": v(0.2, 16.07) * mm, "end": v(4.96, 16.07) * mm});
            skLineSegment(sketch, "E323", {"start": v(4.96, 16.07) * mm, "end": v(4.96, 15.68) * mm});
            skLineSegment(sketch, "E324", {"start": v(4.96, 15.68) * mm, "end": v(0.2, 15.68) * mm});
            skLineSegment(sketch, "E325", {"start": v(0.2, 15.68) * mm, "end": v(0.2, 14.49) * mm});
            skLineSegment(sketch, "E326", {"start": v(0.2, 14.49) * mm, "end": v(1.79, 14.49) * mm});
            skLineSegment(sketch, "E327", {"start": v(1.79, 14.49) * mm, "end": v(1.79, 4.56) * mm});
            skLineSegment(sketch, "E328", {"start": v(1.79, 4.56) * mm, "end": v(1.39, 4.56) * mm});
            skLineSegment(sketch, "E329", {"start": v(-0.2, -0.2) * mm, "end": v(-0.2, 8.14) * mm});
            skLineSegment(sketch, "E330", {"start": v(0.2, 8.14) * mm, "end": v(0.2, 3.37) * mm});
            skLineSegment(sketch, "E331", {"start": v(0.2, 3.37) * mm, "end": v(1.79, 3.37) * mm});
            skLineSegment(sketch, "E332", {"start": v(1.79, 3.37) * mm, "end": v(1.79, 2.98) * mm});
            skLineSegment(sketch, "E333", {"start": v(1.79, 2.98) * mm, "end": v(0.2, 2.98) * mm});
            skLineSegment(sketch, "E334", {"start": v(0.2, 2.98) * mm, "end": v(0.2, 0.2) * mm});
            skLineSegment(sketch, "E335", {"start": v(0.2, 0.2) * mm, "end": v(4.56, 0.2) * mm});
            skLineSegment(sketch, "E336", {"start": v(4.56, 0.2) * mm, "end": v(4.56, 1.39) * mm});
            skLineSegment(sketch, "E337", {"start": v(4.56, 1.39) * mm, "end": v(1.39, 1.39) * mm});
            skLineSegment(sketch, "E338", {"start": v(1.39, 1.39) * mm, "end": v(1.39, 1.79) * mm});
            skLineSegment(sketch, "E339", {"start": v(1.39, 1.79) * mm, "end": v(4.56, 1.79) * mm});
            skLineSegment(sketch, "E340", {"start": v(4.56, 1.79) * mm, "end": v(4.56, 2.98) * mm});
            skLineSegment(sketch, "E341", {"start": v(4.56, 2.98) * mm, "end": v(2.98, 2.98) * mm});
            skLineSegment(sketch, "E342", {"start": v(2.98, 2.98) * mm, "end": v(2.98, 8.14) * mm});
            skLineSegment(sketch, "E343", {"start": v(2.98, 8.14) * mm, "end": v(6.55, 8.14) * mm});
            skLineSegment(sketch, "E344", {"start": v(6.55, 8.14) * mm, "end": v(6.55, 6.55) * mm});
            skLineSegment(sketch, "E345", {"start": v(6.55, 6.55) * mm, "end": v(8.14, 6.55) * mm});
            skLineSegment(sketch, "E346", {"start": v(8.14, 6.55) * mm, "end": v(8.14, 2.98) * mm});
            skLineSegment(sketch, "E347", {"start": v(8.14, 2.98) * mm, "end": v(6.55, 2.98) * mm});
            skLineSegment(sketch, "E348", {"start": v(6.55, 2.98) * mm, "end": v(6.55, 1.79) * mm});
            skLineSegment(sketch, "E349", {"start": v(6.55, 1.79) * mm, "end": v(10.91, 1.79) * mm});
            skLineSegment(sketch, "E350", {"start": v(10.91, 1.79) * mm, "end": v(10.91, 2.98) * mm});
            skLineSegment(sketch, "E351", {"start": v(10.91, 2.98) * mm, "end": v(9.33, 2.98) * mm});
            skLineSegment(sketch, "E352", {"start": v(9.33, 2.98) * mm, "end": v(9.33, 7.74) * mm});
            skLineSegment(sketch, "E353", {"start": v(9.33, 7.74) * mm, "end": v(7.74, 7.74) * mm});
            skLineSegment(sketch, "E354", {"start": v(7.74, 7.74) * mm, "end": v(7.74, 9.72) * mm});
            skLineSegment(sketch, "E355", {"start": v(7.74, 9.72) * mm, "end": v(9.33, 9.72) * mm});
            skLineSegment(sketch, "E356", {"start": v(9.33, 9.72) * mm, "end": v(9.33, 14.09) * mm});
            skLineSegment(sketch, "E357", {"start": v(9.33, 14.09) * mm, "end": v(7.74, 14.09) * mm});
            skLineSegment(sketch, "E358", {"start": v(7.74, 14.09) * mm, "end": v(7.74, 15.68) * mm});
            skLineSegment(sketch, "E359", {"start": v(7.74, 15.68) * mm, "end": v(6.15, 15.68) * mm});
            skLineSegment(sketch, "E360", {"start": v(6.15, 15.68) * mm, "end": v(6.15, 16.07) * mm});
            skLineSegment(sketch, "E361", {"start": v(6.15, 16.07) * mm, "end": v(8.14, 16.07) * mm});
            skLineSegment(sketch, "E362", {"start": v(8.14, 16.07) * mm, "end": v(8.14, 14.49) * mm});
            skLineSegment(sketch, "E363", {"start": v(8.14, 14.49) * mm, "end": v(9.72, 14.49) * mm});
            skLineSegment(sketch, "E364", {"start": v(9.72, 14.49) * mm, "end": v(9.72, 9.33) * mm});
            skLineSegment(sketch, "E365", {"start": v(9.72, 9.33) * mm, "end": v(8.14, 9.33) * mm});
            skLineSegment(sketch, "E366", {"start": v(8.14, 9.33) * mm, "end": v(8.14, 8.14) * mm});
            skLineSegment(sketch, "E367", {"start": v(8.14, 8.14) * mm, "end": v(9.72, 8.14) * mm});
            skLineSegment(sketch, "E368", {"start": v(9.72, 8.14) * mm, "end": v(9.72, 3.37) * mm});
            skLineSegment(sketch, "E369", {"start": v(9.72, 3.37) * mm, "end": v(10.91, 3.37) * mm});
            skLineSegment(sketch, "E370", {"start": v(10.91, 3.37) * mm, "end": v(10.91, 8.14) * mm});
            skLineSegment(sketch, "E371", {"start": v(10.91, 8.14) * mm, "end": v(11.31, 8.14) * mm});
            skLineSegment(sketch, "E372", {"start": v(11.31, 8.14) * mm, "end": v(11.31, -0.2) * mm});
            skLineSegment(sketch, "E373", {"start": v(11.31, -0.2) * mm, "end": v(10.91, -0.2) * mm});
            skLineSegment(sketch, "E374", {"start": v(2.98, 9.33) * mm, "end": v(2.98, 9.72) * mm});
            skLineSegment(sketch, "E375", {"start": v(2.98, 9.72) * mm, "end": v(6.15, 9.72) * mm});
            skLineSegment(sketch, "E376", {"start": v(6.15, 9.72) * mm, "end": v(6.15, 11.31) * mm});
            skLineSegment(sketch, "E377", {"start": v(6.15, 11.31) * mm, "end": v(7.74, 11.31) * mm});
            skLineSegment(sketch, "E378", {"start": v(7.74, 11.31) * mm, "end": v(7.74, 12.5) * mm});
            skLineSegment(sketch, "E379", {"start": v(7.74, 12.5) * mm, "end": v(6.15, 12.5) * mm});
            skLineSegment(sketch, "E380", {"start": v(6.15, 12.5) * mm, "end": v(6.15, 14.09) * mm});
            skLineSegment(sketch, "E381", {"start": v(6.15, 14.09) * mm, "end": v(3.37, 14.09) * mm});
            skLineSegment(sketch, "E382", {"start": v(3.37, 14.09) * mm, "end": v(3.37, 12.9) * mm});
            skLineSegment(sketch, "E383", {"start": v(3.37, 12.9) * mm, "end": v(4.96, 12.9) * mm});
            skLineSegment(sketch, "E384", {"start": v(4.96, 12.9) * mm, "end": v(4.96, 10.91) * mm});
            skLineSegment(sketch, "E385", {"start": v(4.96, 10.91) * mm, "end": v(4.56, 10.91) * mm});
            skLineSegment(sketch, "E386", {"start": v(4.56, 10.91) * mm, "end": v(4.56, 12.5) * mm});
            skLineSegment(sketch, "E387", {"start": v(4.56, 12.5) * mm, "end": v(3.37, 12.5) * mm});
            skLineSegment(sketch, "E388", {"start": v(3.37, 12.5) * mm, "end": v(3.37, 10.91) * mm});
            skLineSegment(sketch, "E389", {"start": v(3.37, 10.91) * mm, "end": v(2.98, 10.91) * mm});
            skLineSegment(sketch, "E390", {"start": v(2.98, 10.91) * mm, "end": v(2.98, 14.49) * mm});
            skLineSegment(sketch, "E391", {"start": v(2.98, 14.49) * mm, "end": v(6.55, 14.49) * mm});
            skLineSegment(sketch, "E392", {"start": v(6.55, 14.49) * mm, "end": v(6.55, 12.9) * mm});
            skLineSegment(sketch, "E393", {"start": v(6.55, 12.9) * mm, "end": v(8.14, 12.9) * mm});
            skLineSegment(sketch, "E394", {"start": v(8.14, 12.9) * mm, "end": v(8.14, 10.91) * mm});
            skLineSegment(sketch, "E395", {"start": v(8.14, 10.91) * mm, "end": v(6.55, 10.91) * mm});
            skLineSegment(sketch, "E396", {"start": v(6.55, 10.91) * mm, "end": v(6.55, 9.33) * mm});
            skLineSegment(sketch, "E397", {"start": v(6.55, 9.33) * mm, "end": v(2.98, 9.33) * mm});
            skLineSegment(sketch, "E398", {"start": v(10.91, 0.2) * mm, "end": v(10.91, 1.39) * mm});
            skLineSegment(sketch, "E399", {"start": v(10.91, 1.39) * mm, "end": v(6.15, 1.39) * mm});
            skLineSegment(sketch, "E400", {"start": v(6.15, 1.39) * mm, "end": v(6.15, 3.37) * mm});
            skLineSegment(sketch, "E401", {"start": v(6.15, 3.37) * mm, "end": v(7.74, 3.37) * mm});
            skLineSegment(sketch, "E402", {"start": v(7.74, 3.37) * mm, "end": v(7.74, 6.15) * mm});
            skLineSegment(sketch, "E403", {"start": v(7.74, 6.15) * mm, "end": v(6.15, 6.15) * mm});
            skLineSegment(sketch, "E404", {"start": v(6.15, 6.15) * mm, "end": v(6.15, 7.74) * mm});
            skLineSegment(sketch, "E405", {"start": v(6.15, 7.74) * mm, "end": v(3.37, 7.74) * mm});
            skLineSegment(sketch, "E406", {"start": v(3.37, 7.74) * mm, "end": v(3.37, 4.96) * mm});
            skLineSegment(sketch, "E407", {"start": v(3.37, 4.96) * mm, "end": v(4.56, 4.96) * mm});
            skLineSegment(sketch, "E408", {"start": v(4.56, 4.96) * mm, "end": v(4.56, 6.55) * mm});
            skLineSegment(sketch, "E409", {"start": v(4.56, 6.55) * mm, "end": v(4.96, 6.55) * mm});
            skLineSegment(sketch, "E410", {"start": v(4.96, 6.55) * mm, "end": v(4.96, 4.96) * mm});
            skLineSegment(sketch, "E411", {"start": v(4.96, 4.96) * mm, "end": v(6.55, 4.96) * mm});
            skLineSegment(sketch, "E412", {"start": v(6.55, 4.96) * mm, "end": v(6.55, 4.56) * mm});
            skLineSegment(sketch, "E413", {"start": v(6.55, 4.56) * mm, "end": v(3.37, 4.56) * mm});
            skLineSegment(sketch, "E414", {"start": v(3.37, 4.56) * mm, "end": v(3.37, 3.37) * mm});
            skLineSegment(sketch, "E415", {"start": v(3.37, 3.37) * mm, "end": v(4.96, 3.37) * mm});
            skLineSegment(sketch, "E416", {"start": v(4.96, 3.37) * mm, "end": v(4.96, 0.2) * mm});
            skLineSegment(sketch, "E417", {"start": v(4.96, 0.2) * mm, "end": v(9.67, 0.2) * mm});
            skLineSegment(sketch, "E418", {"start": v(15.68, 1.39) * mm, "end": v(15.68, 1.79) * mm});
            skLineSegment(sketch, "E419", {"start": v(15.68, 1.79) * mm, "end": v(20.44, 1.79) * mm});
            skLineSegment(sketch, "E420", {"start": v(20.44, 1.79) * mm, "end": v(20.44, 4.56) * mm});
            skLineSegment(sketch, "E421", {"start": v(20.44, 4.56) * mm, "end": v(19.25, 4.56) * mm});
            skLineSegment(sketch, "E422", {"start": v(19.25, 4.56) * mm, "end": v(19.25, 2.98) * mm});
            skLineSegment(sketch, "E423", {"start": v(19.25, 2.98) * mm, "end": v(14.09, 2.98) * mm});
            skLineSegment(sketch, "E424", {"start": v(14.09, 2.98) * mm, "end": v(14.09, 8.14) * mm});
            skLineSegment(sketch, "E425", {"start": v(14.09, 8.14) * mm, "end": v(17.66, 8.14) * mm});
            skLineSegment(sketch, "E426", {"start": v(17.66, 8.14) * mm, "end": v(17.66, 6.55) * mm});
            skLineSegment(sketch, "E427", {"start": v(17.66, 6.55) * mm, "end": v(18.85, 6.55) * mm});
            skLineSegment(sketch, "E428", {"start": v(18.85, 6.55) * mm, "end": v(18.85, 10.91) * mm});
            skLineSegment(sketch, "E429", {"start": v(18.85, 10.91) * mm, "end": v(17.66, 10.91) * mm});
            skLineSegment(sketch, "E430", {"start": v(17.66, 10.91) * mm, "end": v(17.66, 9.33) * mm});
            skLineSegment(sketch, "E431", {"start": v(17.66, 9.33) * mm, "end": v(14.09, 9.33) * mm});
            skLineSegment(sketch, "E432", {"start": v(14.09, 9.33) * mm, "end": v(14.09, 14.49) * mm});
            skLineSegment(sketch, "E433", {"start": v(14.09, 14.49) * mm, "end": v(19.25, 14.49) * mm});
            skLineSegment(sketch, "E434", {"start": v(19.25, 14.49) * mm, "end": v(19.25, 12.9) * mm});
            skLineSegment(sketch, "E435", {"start": v(19.25, 12.9) * mm, "end": v(20.44, 12.9) * mm});
            skLineSegment(sketch, "E436", {"start": v(20.44, 12.9) * mm, "end": v(20.44, 15.68) * mm});
            skLineSegment(sketch, "E437", {"start": v(20.44, 15.68) * mm, "end": v(11.31, 15.68) * mm});
            skLineSegment(sketch, "E438", {"start": v(11.31, 15.68) * mm, "end": v(11.31, 14.49) * mm});
            skLineSegment(sketch, "E439", {"start": v(11.31, 14.49) * mm, "end": v(12.9, 14.49) * mm});
            skLineSegment(sketch, "E440", {"start": v(12.9, 14.49) * mm, "end": v(12.9, 14.09) * mm});
            skLineSegment(sketch, "E441", {"start": v(12.9, 14.09) * mm, "end": v(11.31, 14.09) * mm});
            skLineSegment(sketch, "E442", {"start": v(11.31, 14.09) * mm, "end": v(11.31, 9.33) * mm});
            skLineSegment(sketch, "E443", {"start": v(10.91, 9.33) * mm, "end": v(10.91, 17.66) * mm});
            skLineSegment(sketch, "E444", {"start": v(10.91, 17.66) * mm, "end": v(22.42, 17.66) * mm});
            skLineSegment(sketch, "E445", {"start": v(22.42, 17.66) * mm, "end": v(22.42, 9.33) * mm});
            skLineSegment(sketch, "E446", {"start": v(22.42, 9.33) * mm, "end": v(20.84, 9.33) * mm});
            skLineSegment(sketch, "E447", {"start": v(20.84, 9.33) * mm, "end": v(20.84, 7.74) * mm});
            skLineSegment(sketch, "E448", {"start": v(20.84, 7.74) * mm, "end": v(20.44, 7.74) * mm});
            skLineSegment(sketch, "E449", {"start": v(20.44, 7.74) * mm, "end": v(20.44, 9.72) * mm});
            skLineSegment(sketch, "E450", {"start": v(20.44, 9.72) * mm, "end": v(22.03, 9.72) * mm});
            skLineSegment(sketch, "E451", {"start": v(22.03, 9.72) * mm, "end": v(22.03, 17.26) * mm});
            skLineSegment(sketch, "E452", {"start": v(22.03, 17.26) * mm, "end": v(19.25, 17.26) * mm});
            skLineSegment(sketch, "E453", {"start": v(19.25, 17.26) * mm, "end": v(19.25, 16.07) * mm});
            skLineSegment(sketch, "E454", {"start": v(19.25, 16.07) * mm, "end": v(20.84, 16.07) * mm});
            skLineSegment(sketch, "E455", {"start": v(20.84, 16.07) * mm, "end": v(20.84, 10.91) * mm});
            skLineSegment(sketch, "E456", {"start": v(20.84, 10.91) * mm, "end": v(20.44, 10.91) * mm});
            skLineSegment(sketch, "E457", {"start": v(20.44, 10.91) * mm, "end": v(20.44, 12.5) * mm});
            skLineSegment(sketch, "E458", {"start": v(20.44, 12.5) * mm, "end": v(18.85, 12.5) * mm});
            skLineSegment(sketch, "E459", {"start": v(18.85, 12.5) * mm, "end": v(18.85, 14.09) * mm});
            skLineSegment(sketch, "E460", {"start": v(18.85, 14.09) * mm, "end": v(17.66, 14.09) * mm});
            skLineSegment(sketch, "E461", {"start": v(17.66, 14.09) * mm, "end": v(17.66, 12.5) * mm});
            skLineSegment(sketch, "E462", {"start": v(17.66, 12.5) * mm, "end": v(17.26, 12.5) * mm});
            skLineSegment(sketch, "E463", {"start": v(17.26, 12.5) * mm, "end": v(17.26, 14.09) * mm});
            skLineSegment(sketch, "E464", {"start": v(17.26, 14.09) * mm, "end": v(14.49, 14.09) * mm});
            skLineSegment(sketch, "E465", {"start": v(14.49, 14.09) * mm, "end": v(14.49, 11.31) * mm});
            skLineSegment(sketch, "E466", {"start": v(14.49, 11.31) * mm, "end": v(15.68, 11.31) * mm});
            skLineSegment(sketch, "E467", {"start": v(15.68, 11.31) * mm, "end": v(15.68, 12.9) * mm});
            skLineSegment(sketch, "E468", {"start": v(15.68, 12.9) * mm, "end": v(16.07, 12.9) * mm});
            skLineSegment(sketch, "E469", {"start": v(16.07, 12.9) * mm, "end": v(16.07, 10.91) * mm});
            skLineSegment(sketch, "E470", {"start": v(16.07, 10.91) * mm, "end": v(14.49, 10.91) * mm});
            skLineSegment(sketch, "E471", {"start": v(14.49, 10.91) * mm, "end": v(14.49, 9.72) * mm});
            skLineSegment(sketch, "E472", {"start": v(14.49, 9.72) * mm, "end": v(17.26, 9.72) * mm});
            skLineSegment(sketch, "E473", {"start": v(17.26, 9.72) * mm, "end": v(17.26, 11.31) * mm});
            skLineSegment(sketch, "E474", {"start": v(17.26, 11.31) * mm, "end": v(19.25, 11.31) * mm});
            skLineSegment(sketch, "E475", {"start": v(19.25, 11.31) * mm, "end": v(19.25, 6.15) * mm});
            skLineSegment(sketch, "E476", {"start": v(19.25, 6.15) * mm, "end": v(15.68, 6.15) * mm});
            skLineSegment(sketch, "E477", {"start": v(15.68, 6.15) * mm, "end": v(15.68, 6.55) * mm});
            skLineSegment(sketch, "E478", {"start": v(15.68, 6.55) * mm, "end": v(17.26, 6.55) * mm});
            skLineSegment(sketch, "E479", {"start": v(17.26, 6.55) * mm, "end": v(17.26, 7.74) * mm});
            skLineSegment(sketch, "E480", {"start": v(17.26, 7.74) * mm, "end": v(14.49, 7.74) * mm});
            skLineSegment(sketch, "E481", {"start": v(14.49, 7.74) * mm, "end": v(14.49, 4.96) * mm});
            skLineSegment(sketch, "E482", {"start": v(14.49, 4.96) * mm, "end": v(17.66, 4.96) * mm});
            skLineSegment(sketch, "E483", {"start": v(17.66, 4.96) * mm, "end": v(17.66, 4.56) * mm});
            skLineSegment(sketch, "E484", {"start": v(17.66, 4.56) * mm, "end": v(14.49, 4.56) * mm});
            skLineSegment(sketch, "E485", {"start": v(14.49, 4.56) * mm, "end": v(14.49, 3.37) * mm});
            skLineSegment(sketch, "E486", {"start": v(14.49, 3.37) * mm, "end": v(18.85, 3.37) * mm});
            skLineSegment(sketch, "E487", {"start": v(18.85, 3.37) * mm, "end": v(18.85, 4.96) * mm});
            skLineSegment(sketch, "E488", {"start": v(18.85, 4.96) * mm, "end": v(20.84, 4.96) * mm});
            skLineSegment(sketch, "E489", {"start": v(20.84, 4.96) * mm, "end": v(20.84, 1.39) * mm});
            skLineSegment(sketch, "E490", {"start": v(20.84, 1.39) * mm, "end": v(15.68, 1.39) * mm});
            skLineSegment(sketch, "E491", {"start": v(10.91, -0.2) * mm, "end": v(10.91, 8.14) * mm});
            skLineSegment(sketch, "E492", {"start": v(11.31, 8.14) * mm, "end": v(11.31, 3.37) * mm});
            skLineSegment(sketch, "E493", {"start": v(11.31, 3.37) * mm, "end": v(12.5, 3.37) * mm});
            skLineSegment(sketch, "E494", {"start": v(12.5, 3.37) * mm, "end": v(12.5, 12.9) * mm});
            skLineSegment(sketch, "E495", {"start": v(12.5, 12.9) * mm, "end": v(12.9, 12.9) * mm});
            skLineSegment(sketch, "E496", {"start": v(12.9, 12.9) * mm, "end": v(12.9, 2.98) * mm});
            skLineSegment(sketch, "E497", {"start": v(12.9, 2.98) * mm, "end": v(11.31, 2.98) * mm});
            skLineSegment(sketch, "E498", {"start": v(11.31, 2.98) * mm, "end": v(11.31, 1.79) * mm});
            skLineSegment(sketch, "E499", {"start": v(11.31, 1.79) * mm, "end": v(14.49, 1.79) * mm});
            skLineSegment(sketch, "E500", {"start": v(14.49, 1.79) * mm, "end": v(14.49, 1.39) * mm});
            skLineSegment(sketch, "E501", {"start": v(14.49, 1.39) * mm, "end": v(11.31, 1.39) * mm});
            skLineSegment(sketch, "E502", {"start": v(11.31, 1.39) * mm, "end": v(11.31, 0.2) * mm});
            skLineSegment(sketch, "E503", {"start": v(11.31, 0.2) * mm, "end": v(22.03, 0.2) * mm});
            skLineSegment(sketch, "E504", {"start": v(22.03, 0.2) * mm, "end": v(22.03, 6.15) * mm});
            skLineSegment(sketch, "E505", {"start": v(22.03, 6.15) * mm, "end": v(20.44, 6.15) * mm});
            skLineSegment(sketch, "E506", {"start": v(20.44, 6.15) * mm, "end": v(20.44, 6.55) * mm});
            skLineSegment(sketch, "E507", {"start": v(20.44, 6.55) * mm, "end": v(22.03, 6.55) * mm});
            skLineSegment(sketch, "E508", {"start": v(22.03, 6.55) * mm, "end": v(22.03, 8.14) * mm});
            skLineSegment(sketch, "E509", {"start": v(22.03, 8.14) * mm, "end": v(22.42, 8.14) * mm});
            skLineSegment(sketch, "E510", {"start": v(22.42, 8.14) * mm, "end": v(22.42, -0.2) * mm});
            skLineSegment(sketch, "E511", {"start": v(22.42, -0.2) * mm, "end": v(10.91, -0.2) * mm});
            skLineSegment(sketch, "E512", {"start": v(18.85, 16.07) * mm, "end": v(18.85, 17.26) * mm});
            skLineSegment(sketch, "E513", {"start": v(18.85, 17.26) * mm, "end": v(11.31, 17.26) * mm});
            skLineSegment(sketch, "E514", {"start": v(11.31, 17.26) * mm, "end": v(11.31, 16.07) * mm});
            skLineSegment(sketch, "E515", {"start": v(11.31, 16.07) * mm, "end": v(18.85, 16.07) * mm});
            skLineSegment(sketch, "E516", {"start": v(23.61, 1.39) * mm, "end": v(23.61, 1.79) * mm});
            skLineSegment(sketch, "E517", {"start": v(23.61, 1.79) * mm, "end": v(29.96, 1.79) * mm});
            skLineSegment(sketch, "E518", {"start": v(29.96, 1.79) * mm, "end": v(29.96, 3.37) * mm});
            skLineSegment(sketch, "E519", {"start": v(29.96, 3.37) * mm, "end": v(31.55, 3.37) * mm});
            skLineSegment(sketch, "E520", {"start": v(31.55, 3.37) * mm, "end": v(31.55, 14.09) * mm});
            skLineSegment(sketch, "E521", {"start": v(31.55, 14.09) * mm, "end": v(29.96, 14.09) * mm});
            skLineSegment(sketch, "E522", {"start": v(29.96, 14.09) * mm, "end": v(29.96, 15.68) * mm});
            skLineSegment(sketch, "E523", {"start": v(29.96, 15.68) * mm, "end": v(23.61, 15.68) * mm});
            skLineSegment(sketch, "E524", {"start": v(23.61, 15.68) * mm, "end": v(23.61, 16.07) * mm});
            skLineSegment(sketch, "E525", {"start": v(23.61, 16.07) * mm, "end": v(28.38, 16.07) * mm});
            skLineSegment(sketch, "E526", {"start": v(28.38, 16.07) * mm, "end": v(28.38, 17.26) * mm});
            skLineSegment(sketch, "E527", {"start": v(28.38, 17.26) * mm, "end": v(22.42, 17.26) * mm});
            skLineSegment(sketch, "E528", {"start": v(22.42, 17.26) * mm, "end": v(22.42, 14.49) * mm});
            skLineSegment(sketch, "E529", {"start": v(22.42, 14.49) * mm, "end": v(24.01, 14.49) * mm});
            skLineSegment(sketch, "E530", {"start": v(24.01, 14.49) * mm, "end": v(24.01, 6.15) * mm});
            skLineSegment(sketch, "E531", {"start": v(24.01, 6.15) * mm, "end": v(23.61, 6.15) * mm});
            skLineSegment(sketch, "E532", {"start": v(23.61, 6.15) * mm, "end": v(23.61, 14.09) * mm});
            skLineSegment(sketch, "E533", {"start": v(23.61, 14.09) * mm, "end": v(22.42, 14.09) * mm});
            skLineSegment(sketch, "E534", {"start": v(22.42, 14.09) * mm, "end": v(22.42, 9.33) * mm});
            skLineSegment(sketch, "E535", {"start": v(22.42, 9.33) * mm, "end": v(22.03, 9.33) * mm});
            skLineSegment(sketch, "E536", {"start": v(22.03, 9.33) * mm, "end": v(22.03, 17.66) * mm});
            skLineSegment(sketch, "E537", {"start": v(22.03, 17.66) * mm, "end": v(33.54, 17.66) * mm});
            skLineSegment(sketch, "E538", {"start": v(33.54, 17.66) * mm, "end": v(33.54, 9.33) * mm});
            skLineSegment(sketch, "E539", {"start": v(33.54, 9.33) * mm, "end": v(31.95, 9.33) * mm});
            skLineSegment(sketch, "E540", {"start": v(31.95, 9.33) * mm, "end": v(31.95, 2.98) * mm});
            skLineSegment(sketch, "E541", {"start": v(31.95, 2.98) * mm, "end": v(30.36, 2.98) * mm});
            skLineSegment(sketch, "E542", {"start": v(30.36, 2.98) * mm, "end": v(30.36, 1.39) * mm});
            skLineSegment(sketch, "E543", {"start": v(30.36, 1.39) * mm, "end": v(23.61, 1.39) * mm});
            skLineSegment(sketch, "E544", {"start": v(22.03, -0.2) * mm, "end": v(22.03, 8.14) * mm});
            skLineSegment(sketch, "E545", {"start": v(22.42, 8.14) * mm, "end": v(22.42, 3.37) * mm});
            skLineSegment(sketch, "E546", {"start": v(22.42, 3.37) * mm, "end": v(23.61, 3.37) * mm});
            skLineSegment(sketch, "E547", {"start": v(23.61, 3.37) * mm, "end": v(23.61, 4.96) * mm});
            skLineSegment(sketch, "E548", {"start": v(23.61, 4.96) * mm, "end": v(24.01, 4.96) * mm});
            skLineSegment(sketch, "E549", {"start": v(24.01, 4.96) * mm, "end": v(24.01, 2.98) * mm});
            skLineSegment(sketch, "E550", {"start": v(24.01, 2.98) * mm, "end": v(22.42, 2.98) * mm});
            skLineSegment(sketch, "E551", {"start": v(22.42, 2.98) * mm, "end": v(22.42, 0.2) * mm});
            skLineSegment(sketch, "E552", {"start": v(22.42, 0.2) * mm, "end": v(31.55, 0.2) * mm});
            skLineSegment(sketch, "E553", {"start": v(31.55, 0.2) * mm, "end": v(31.55, 1.79) * mm});
            skLineSegment(sketch, "E554", {"start": v(31.55, 1.79) * mm, "end": v(31.95, 1.79) * mm});
            skLineSegment(sketch, "E555", {"start": v(31.95, 1.79) * mm, "end": v(31.95, 0.2) * mm});
            skLineSegment(sketch, "E556", {"start": v(31.95, 0.2) * mm, "end": v(33.14, 0.2) * mm});
            skLineSegment(sketch, "E557", {"start": v(33.14, 0.2) * mm, "end": v(33.14, 8.14) * mm});
            skLineSegment(sketch, "E558", {"start": v(33.14, 8.14) * mm, "end": v(33.54, 8.14) * mm});
            skLineSegment(sketch, "E559", {"start": v(33.54, 8.14) * mm, "end": v(33.54, -0.2) * mm});
            skLineSegment(sketch, "E560", {"start": v(33.54, -0.2) * mm, "end": v(22.03, -0.2) * mm});
            skLineSegment(sketch, "E561", {"start": v(25.2, 2.98) * mm, "end": v(25.2, 11.31) * mm});
            skLineSegment(sketch, "E562", {"start": v(25.2, 11.31) * mm, "end": v(25.6, 11.31) * mm});
            skLineSegment(sketch, "E563", {"start": v(25.6, 11.31) * mm, "end": v(25.6, 9.72) * mm});
            skLineSegment(sketch, "E564", {"start": v(25.6, 9.72) * mm, "end": v(28.77, 9.72) * mm});
            skLineSegment(sketch, "E565", {"start": v(28.77, 9.72) * mm, "end": v(28.77, 7.74) * mm});
            skLineSegment(sketch, "E566", {"start": v(28.77, 7.74) * mm, "end": v(28.38, 7.74) * mm});
            skLineSegment(sketch, "E567", {"start": v(28.38, 7.74) * mm, "end": v(28.38, 9.33) * mm});
            skLineSegment(sketch, "E568", {"start": v(28.38, 9.33) * mm, "end": v(25.6, 9.33) * mm});
            skLineSegment(sketch, "E569", {"start": v(25.6, 9.33) * mm, "end": v(25.6, 4.96) * mm});
            skLineSegment(sketch, "E570", {"start": v(25.6, 4.96) * mm, "end": v(26.79, 4.96) * mm});
            skLineSegment(sketch, "E571", {"start": v(26.79, 4.96) * mm, "end": v(26.79, 8.14) * mm});
            skLineSegment(sketch, "E572", {"start": v(26.79, 8.14) * mm, "end": v(27.19, 8.14) * mm});
            skLineSegment(sketch, "E573", {"start": v(27.19, 8.14) * mm, "end": v(27.19, 6.55) * mm});
            skLineSegment(sketch, "E574", {"start": v(27.19, 6.55) * mm, "end": v(28.77, 6.55) * mm});
            skLineSegment(sketch, "E575", {"start": v(28.77, 6.55) * mm, "end": v(28.77, 6.15) * mm});
            skLineSegment(sketch, "E576", {"start": v(28.77, 6.15) * mm, "end": v(27.19, 6.15) * mm});
            skLineSegment(sketch, "E577", {"start": v(27.19, 6.15) * mm, "end": v(27.19, 4.56) * mm});
            skLineSegment(sketch, "E578", {"start": v(27.19, 4.56) * mm, "end": v(25.6, 4.56) * mm});
            skLineSegment(sketch, "E579", {"start": v(25.6, 4.56) * mm, "end": v(25.6, 3.37) * mm});
            skLineSegment(sketch, "E580", {"start": v(25.6, 3.37) * mm, "end": v(28.38, 3.37) * mm});
            skLineSegment(sketch, "E581", {"start": v(28.38, 3.37) * mm, "end": v(28.38, 4.96) * mm});
            skLineSegment(sketch, "E582", {"start": v(28.38, 4.96) * mm, "end": v(29.96, 4.96) * mm});
            skLineSegment(sketch, "E583", {"start": v(29.96, 4.96) * mm, "end": v(29.96, 12.5) * mm});
            skLineSegment(sketch, "E584", {"start": v(29.96, 12.5) * mm, "end": v(28.38, 12.5) * mm});
            skLineSegment(sketch, "E585", {"start": v(28.38, 12.5) * mm, "end": v(28.38, 14.09) * mm});
            skLineSegment(sketch, "E586", {"start": v(28.38, 14.09) * mm, "end": v(25.6, 14.09) * mm});
            skLineSegment(sketch, "E587", {"start": v(25.6, 14.09) * mm, "end": v(25.6, 12.5) * mm});
            skLineSegment(sketch, "E588", {"start": v(25.6, 12.5) * mm, "end": v(25.2, 12.5) * mm});
            skLineSegment(sketch, "E589", {"start": v(25.2, 12.5) * mm, "end": v(25.2, 14.49) * mm});
            skLineSegment(sketch, "E590", {"start": v(25.2, 14.49) * mm, "end": v(28.77, 14.49) * mm});
            skLineSegment(sketch, "E591", {"start": v(28.77, 14.49) * mm, "end": v(28.77, 12.9) * mm});
            skLineSegment(sketch, "E592", {"start": v(28.77, 12.9) * mm, "end": v(30.36, 12.9) * mm});
            skLineSegment(sketch, "E593", {"start": v(30.36, 12.9) * mm, "end": v(30.36, 4.56) * mm});
            skLineSegment(sketch, "E594", {"start": v(30.36, 4.56) * mm, "end": v(28.77, 4.56) * mm});
            skLineSegment(sketch, "E595", {"start": v(28.77, 4.56) * mm, "end": v(28.77, 2.98) * mm});
            skLineSegment(sketch, "E596", {"start": v(28.77, 2.98) * mm, "end": v(25.2, 2.98) * mm});
            skLineSegment(sketch, "E597", {"start": v(26.79, 10.91) * mm, "end": v(26.79, 12.9) * mm});
            skLineSegment(sketch, "E598", {"start": v(26.79, 12.9) * mm, "end": v(27.19, 12.9) * mm});
            skLineSegment(sketch, "E599", {"start": v(27.19, 12.9) * mm, "end": v(27.19, 11.31) * mm});
            skLineSegment(sketch, "E600", {"start": v(27.19, 11.31) * mm, "end": v(28.77, 11.31) * mm});
            skLineSegment(sketch, "E601", {"start": v(28.77, 11.31) * mm, "end": v(28.77, 10.91) * mm});
            skLineSegment(sketch, "E602", {"start": v(28.77, 10.91) * mm, "end": v(26.79, 10.91) * mm});
            skLineSegment(sketch, "E603", {"start": v(33.14, 9.72) * mm, "end": v(33.14, 15.68) * mm});
            skLineSegment(sketch, "E604", {"start": v(33.14, 15.68) * mm, "end": v(31.55, 15.68) * mm});
            skLineSegment(sketch, "E605", {"start": v(31.55, 15.68) * mm, "end": v(31.55, 16.07) * mm});
            skLineSegment(sketch, "E606", {"start": v(31.55, 16.07) * mm, "end": v(33.14, 16.07) * mm});
            skLineSegment(sketch, "E607", {"start": v(33.14, 16.07) * mm, "end": v(33.14, 17.26) * mm});
            skLineSegment(sketch, "E608", {"start": v(33.14, 17.26) * mm, "end": v(28.77, 17.26) * mm});
            skLineSegment(sketch, "E609", {"start": v(28.77, 17.26) * mm, "end": v(28.77, 16.07) * mm});
            skLineSegment(sketch, "E610", {"start": v(28.77, 16.07) * mm, "end": v(30.36, 16.07) * mm});
            skLineSegment(sketch, "E611", {"start": v(30.36, 16.07) * mm, "end": v(30.36, 14.49) * mm});
            skLineSegment(sketch, "E612", {"start": v(30.36, 14.49) * mm, "end": v(31.95, 14.49) * mm});
            skLineSegment(sketch, "E613", {"start": v(31.95, 14.49) * mm, "end": v(31.95, 9.72) * mm});
            skLineSegment(sketch, "E614", {"start": v(31.95, 9.72) * mm, "end": v(33.14, 9.72) * mm});
            skLineSegment(sketch, "E615", {"start": v(-25.6, -11.31) * mm, "end": v(-25.6, -9.33) * mm});
            skLineSegment(sketch, "E616", {"start": v(-25.6, -9.33) * mm, "end": v(-24.01, -9.33) * mm});
            skLineSegment(sketch, "E617", {"start": v(-24.01, -9.33) * mm, "end": v(-24.01, -6.55) * mm});
            skLineSegment(sketch, "E618", {"start": v(-24.01, -6.55) * mm, "end": v(-25.6, -6.55) * mm});
            skLineSegment(sketch, "E619", {"start": v(-25.6, -6.55) * mm, "end": v(-25.6, -6.15) * mm});
            skLineSegment(sketch, "E620", {"start": v(-25.6, -6.15) * mm, "end": v(-23.61, -6.15) * mm});
            skLineSegment(sketch, "E621", {"start": v(-23.61, -6.15) * mm, "end": v(-23.61, -7.74) * mm});
            skLineSegment(sketch, "E622", {"start": v(-23.61, -7.74) * mm, "end": v(-22.42, -7.74) * mm});
            skLineSegment(sketch, "E623", {"start": v(-22.42, -7.74) * mm, "end": v(-22.42, -0.2) * mm});
            skLineSegment(sketch, "E624", {"start": v(-22.42, -0.2) * mm, "end": v(-33.14, -0.2) * mm});
            skLineSegment(sketch, "E625", {"start": v(-33.14, -0.2) * mm, "end": v(-33.14, -2.98) * mm});
            skLineSegment(sketch, "E626", {"start": v(-33.14, -2.98) * mm, "end": v(-31.95, -2.98) * mm});
            skLineSegment(sketch, "E627", {"start": v(-31.95, -2.98) * mm, "end": v(-31.95, -1.39) * mm});
            skLineSegment(sketch, "E628", {"start": v(-31.95, -1.39) * mm, "end": v(-26.79, -1.39) * mm});
            skLineSegment(sketch, "E629", {"start": v(-26.79, -1.39) * mm, "end": v(-26.79, -1.79) * mm});
            skLineSegment(sketch, "E630", {"start": v(-26.79, -1.79) * mm, "end": v(-31.55, -1.79) * mm});
            skLineSegment(sketch, "E631", {"start": v(-31.55, -1.79) * mm, "end": v(-31.55, -4.56) * mm});
            skLineSegment(sketch, "E632", {"start": v(-31.55, -4.56) * mm, "end": v(-30.36, -4.56) * mm});
            skLineSegment(sketch, "E633", {"start": v(-30.36, -4.56) * mm, "end": v(-30.36, -2.98) * mm});
            skLineSegment(sketch, "E634", {"start": v(-30.36, -2.98) * mm, "end": v(-28.38, -2.98) * mm});
            skLineSegment(sketch, "E635", {"start": v(-28.38, -2.98) * mm, "end": v(-28.38, -6.55) * mm});
            skLineSegment(sketch, "E636", {"start": v(-28.38, -6.55) * mm, "end": v(-28.77, -6.55) * mm});
            skLineSegment(sketch, "E637", {"start": v(-28.77, -6.55) * mm, "end": v(-28.77, -3.37) * mm});
            skLineSegment(sketch, "E638", {"start": v(-28.77, -3.37) * mm, "end": v(-29.96, -3.37) * mm});
            skLineSegment(sketch, "E639", {"start": v(-29.96, -3.37) * mm, "end": v(-29.96, -4.96) * mm});
            skLineSegment(sketch, "E640", {"start": v(-29.96, -4.96) * mm, "end": v(-31.95, -4.96) * mm});
            skLineSegment(sketch, "E641", {"start": v(-31.95, -4.96) * mm, "end": v(-31.95, -3.37) * mm});
            skLineSegment(sketch, "E642", {"start": v(-31.95, -3.37) * mm, "end": v(-33.14, -3.37) * mm});
            skLineSegment(sketch, "E643", {"start": v(-33.14, -3.37) * mm, "end": v(-33.14, -6.15) * mm});
            skLineSegment(sketch, "E644", {"start": v(-33.14, -6.15) * mm, "end": v(-29.96, -6.15) * mm});
            skLineSegment(sketch, "E645", {"start": v(-29.96, -6.15) * mm, "end": v(-29.96, -6.55) * mm});
            skLineSegment(sketch, "E646", {"start": v(-29.96, -6.55) * mm, "end": v(-33.14, -6.55) * mm});
            skLineSegment(sketch, "E647", {"start": v(-33.14, -6.55) * mm, "end": v(-33.14, -7.74) * mm});
            skLineSegment(sketch, "E648", {"start": v(-33.14, -7.74) * mm, "end": v(-29.96, -7.74) * mm});
            skLineSegment(sketch, "E649", {"start": v(-29.96, -7.74) * mm, "end": v(-29.96, -9.72) * mm});
            skLineSegment(sketch, "E650", {"start": v(-29.96, -9.72) * mm, "end": v(-30.36, -9.72) * mm});
            skLineSegment(sketch, "E651", {"start": v(-30.36, -9.72) * mm, "end": v(-30.36, -8.14) * mm});
            skLineSegment(sketch, "E652", {"start": v(-30.36, -8.14) * mm, "end": v(-33.54, -8.14) * mm});
            skLineSegment(sketch, "E653", {"start": v(-33.54, -8.14) * mm, "end": v(-33.54, 0.2) * mm});
            skLineSegment(sketch, "E654", {"start": v(-33.54, 0.2) * mm, "end": v(-22.03, 0.2) * mm});
            skLineSegment(sketch, "E655", {"start": v(-22.03, 0.2) * mm, "end": v(-22.03, -8.14) * mm});
            skLineSegment(sketch, "E656", {"start": v(-22.03, -8.14) * mm, "end": v(-23.61, -8.14) * mm});
            skLineSegment(sketch, "E657", {"start": v(-23.61, -8.14) * mm, "end": v(-23.61, -9.72) * mm});
            skLineSegment(sketch, "E658", {"start": v(-23.61, -9.72) * mm, "end": v(-25.2, -9.72) * mm});
            skLineSegment(sketch, "E659", {"start": v(-25.2, -9.72) * mm, "end": v(-25.2, -11.31) * mm});
            skLineSegment(sketch, "E660", {"start": v(-25.2, -11.31) * mm, "end": v(-25.6, -11.31) * mm});
            skLineSegment(sketch, "E661", {"start": v(-33.54, -17.66) * mm, "end": v(-33.54, -9.33) * mm});
            skLineSegment(sketch, "E662", {"start": v(-33.54, -9.33) * mm, "end": v(-31.55, -9.33) * mm});
            skLineSegment(sketch, "E663", {"start": v(-31.55, -9.33) * mm, "end": v(-31.55, -10.91) * mm});
            skLineSegment(sketch, "E664", {"start": v(-31.55, -10.91) * mm, "end": v(-29.96, -10.91) * mm});
            skLineSegment(sketch, "E665", {"start": v(-29.96, -10.91) * mm, "end": v(-29.96, -12.5) * mm});
            skLineSegment(sketch, "E666", {"start": v(-29.96, -12.5) * mm, "end": v(-28.77, -12.5) * mm});
            skLineSegment(sketch, "E667", {"start": v(-28.77, -12.5) * mm, "end": v(-28.77, -7.74) * mm});
            skLineSegment(sketch, "E668", {"start": v(-28.77, -7.74) * mm, "end": v(-28.38, -7.74) * mm});
            skLineSegment(sketch, "E669", {"start": v(-28.38, -7.74) * mm, "end": v(-28.38, -14.49) * mm});
            skLineSegment(sketch, "E670", {"start": v(-28.38, -14.49) * mm, "end": v(-29.96, -14.49) * mm});
            skLineSegment(sketch, "E671", {"start": v(-29.96, -14.49) * mm, "end": v(-29.96, -15.68) * mm});
            skLineSegment(sketch, "E672", {"start": v(-29.96, -15.68) * mm, "end": v(-28.38, -15.68) * mm});
            skLineSegment(sketch, "E673", {"start": v(-28.38, -15.68) * mm, "end": v(-28.38, -16.07) * mm});
            skLineSegment(sketch, "E674", {"start": v(-28.38, -16.07) * mm, "end": v(-30.36, -16.07) * mm});
            skLineSegment(sketch, "E675", {"start": v(-30.36, -16.07) * mm, "end": v(-30.36, -14.09) * mm});
            skLineSegment(sketch, "E676", {"start": v(-30.36, -14.09) * mm, "end": v(-28.77, -14.09) * mm});
            skLineSegment(sketch, "E677", {"start": v(-28.77, -14.09) * mm, "end": v(-28.77, -12.9) * mm});
            skLineSegment(sketch, "E678", {"start": v(-28.77, -12.9) * mm, "end": v(-31.55, -12.9) * mm});
            skLineSegment(sketch, "E679", {"start": v(-31.55, -12.9) * mm, "end": v(-31.55, -14.49) * mm});
            skLineSegment(sketch, "E680", {"start": v(-31.55, -14.49) * mm, "end": v(-31.95, -14.49) * mm});
            skLineSegment(sketch, "E681", {"start": v(-31.95, -14.49) * mm, "end": v(-31.95, -12.5) * mm});
            skLineSegment(sketch, "E682", {"start": v(-31.95, -12.5) * mm, "end": v(-30.36, -12.5) * mm});
            skLineSegment(sketch, "E683", {"start": v(-30.36, -12.5) * mm, "end": v(-30.36, -11.31) * mm});
            skLineSegment(sketch, "E684", {"start": v(-30.36, -11.31) * mm, "end": v(-31.95, -11.31) * mm});
            skLineSegment(sketch, "E685", {"start": v(-31.95, -11.31) * mm, "end": v(-31.95, -9.72) * mm});
            skLineSegment(sketch, "E686", {"start": v(-31.95, -9.72) * mm, "end": v(-33.14, -9.72) * mm});
            skLineSegment(sketch, "E687", {"start": v(-33.14, -9.72) * mm, "end": v(-33.14, -15.68) * mm});
            skLineSegment(sketch, "E688", {"start": v(-33.14, -15.68) * mm, "end": v(-31.55, -15.68) * mm});
            skLineSegment(sketch, "E689", {"start": v(-31.55, -15.68) * mm, "end": v(-31.55, -16.07) * mm});
            skLineSegment(sketch, "E690", {"start": v(-31.55, -16.07) * mm, "end": v(-33.14, -16.07) * mm});
            skLineSegment(sketch, "E691", {"start": v(-33.14, -16.07) * mm, "end": v(-33.14, -17.26) * mm});
            skLineSegment(sketch, "E692", {"start": v(-33.14, -17.26) * mm, "end": v(-24.01, -17.26) * mm});
            skLineSegment(sketch, "E693", {"start": v(-24.01, -17.26) * mm, "end": v(-24.01, -15.68) * mm});
            skLineSegment(sketch, "E694", {"start": v(-24.01, -15.68) * mm, "end": v(-23.61, -15.68) * mm});
            skLineSegment(sketch, "E695", {"start": v(-23.61, -15.68) * mm, "end": v(-23.61, -17.26) * mm});
            skLineSegment(sketch, "E696", {"start": v(-23.61, -17.26) * mm, "end": v(-22.42, -17.26) * mm});
            skLineSegment(sketch, "E697", {"start": v(-22.42, -17.26) * mm, "end": v(-22.42, -11.31) * mm});
            skLineSegment(sketch, "E698", {"start": v(-22.42, -11.31) * mm, "end": v(-23.61, -11.31) * mm});
            skLineSegment(sketch, "E699", {"start": v(-23.61, -11.31) * mm, "end": v(-23.61, -14.49) * mm});
            skLineSegment(sketch, "E700", {"start": v(-23.61, -14.49) * mm, "end": v(-24.01, -14.49) * mm});
            skLineSegment(sketch, "E701", {"start": v(-24.01, -14.49) * mm, "end": v(-24.01, -12.9) * mm});
            skLineSegment(sketch, "E702", {"start": v(-24.01, -12.9) * mm, "end": v(-26.79, -12.9) * mm});
            skLineSegment(sketch, "E703", {"start": v(-26.79, -12.9) * mm, "end": v(-26.79, -14.09) * mm});
            skLineSegment(sketch, "E704", {"start": v(-26.79, -14.09) * mm, "end": v(-25.2, -14.09) * mm});
            skLineSegment(sketch, "E705", {"start": v(-25.2, -14.09) * mm, "end": v(-25.2, -16.07) * mm});
            skLineSegment(sketch, "E706", {"start": v(-25.2, -16.07) * mm, "end": v(-27.19, -16.07) * mm});
            skLineSegment(sketch, "E707", {"start": v(-27.19, -16.07) * mm, "end": v(-27.19, -15.68) * mm});
            skLineSegment(sketch, "E708", {"start": v(-27.19, -15.68) * mm, "end": v(-25.6, -15.68) * mm});
            skLineSegment(sketch, "E709", {"start": v(-25.6, -15.68) * mm, "end": v(-25.6, -14.49) * mm});
            skLineSegment(sketch, "E710", {"start": v(-25.6, -14.49) * mm, "end": v(-27.19, -14.49) * mm});
            skLineSegment(sketch, "E711", {"start": v(-27.19, -14.49) * mm, "end": v(-27.19, -2.98) * mm});
            skLineSegment(sketch, "E712", {"start": v(-27.19, -2.98) * mm, "end": v(-25.2, -2.98) * mm});
            skLineSegment(sketch, "E713", {"start": v(-25.2, -2.98) * mm, "end": v(-25.2, -4.56) * mm});
            skLineSegment(sketch, "E714", {"start": v(-25.2, -4.56) * mm, "end": v(-24.01, -4.56) * mm});
            skLineSegment(sketch, "E715", {"start": v(-24.01, -4.56) * mm, "end": v(-24.01, -1.79) * mm});
            skLineSegment(sketch, "E716", {"start": v(-24.01, -1.79) * mm, "end": v(-25.6, -1.79) * mm});
            skLineSegment(sketch, "E717", {"start": v(-25.6, -1.79) * mm, "end": v(-25.6, -1.39) * mm});
            skLineSegment(sketch, "E718", {"start": v(-25.6, -1.39) * mm, "end": v(-23.61, -1.39) * mm});
            skLineSegment(sketch, "E719", {"start": v(-23.61, -1.39) * mm, "end": v(-23.61, -4.96) * mm});
            skLineSegment(sketch, "E720", {"start": v(-23.61, -4.96) * mm, "end": v(-25.6, -4.96) * mm});
            skLineSegment(sketch, "E721", {"start": v(-25.6, -4.96) * mm, "end": v(-25.6, -3.37) * mm});
            skLineSegment(sketch, "E722", {"start": v(-25.6, -3.37) * mm, "end": v(-26.79, -3.37) * mm});
            skLineSegment(sketch, "E723", {"start": v(-26.79, -3.37) * mm, "end": v(-26.79, -7.74) * mm});
            skLineSegment(sketch, "E724", {"start": v(-26.79, -7.74) * mm, "end": v(-25.2, -7.74) * mm});
            skLineSegment(sketch, "E725", {"start": v(-25.2, -7.74) * mm, "end": v(-25.2, -8.14) * mm});
            skLineSegment(sketch, "E726", {"start": v(-25.2, -8.14) * mm, "end": v(-26.79, -8.14) * mm});
            skLineSegment(sketch, "E727", {"start": v(-26.79, -8.14) * mm, "end": v(-26.79, -12.5) * mm});
            skLineSegment(sketch, "E728", {"start": v(-26.79, -12.5) * mm, "end": v(-24.01, -12.5) * mm});
            skLineSegment(sketch, "E729", {"start": v(-24.01, -12.5) * mm, "end": v(-24.01, -10.91) * mm});
            skLineSegment(sketch, "E730", {"start": v(-24.01, -10.91) * mm, "end": v(-22.42, -10.91) * mm});
            skLineSegment(sketch, "E731", {"start": v(-22.42, -10.91) * mm, "end": v(-22.42, -9.33) * mm});
            skLineSegment(sketch, "E732", {"start": v(-22.42, -9.33) * mm, "end": v(-22.03, -9.33) * mm});
            skLineSegment(sketch, "E733", {"start": v(-22.03, -9.33) * mm, "end": v(-22.03, -17.66) * mm});
            skLineSegment(sketch, "E734", {"start": v(-22.03, -17.66) * mm, "end": v(-33.54, -17.66) * mm});
            skLineSegment(sketch, "E735", {"start": v(-22.42, -8.14) * mm, "end": v(-22.42, 0.2) * mm});
            skLineSegment(sketch, "E736", {"start": v(-22.42, 0.2) * mm, "end": v(-10.91, 0.2) * mm});
            skLineSegment(sketch, "E737", {"start": v(-10.91, 0.2) * mm, "end": v(-10.91, -8.14) * mm});
            skLineSegment(sketch, "E738", {"start": v(-10.91, -8.14) * mm, "end": v(-11.31, -8.14) * mm});
            skLineSegment(sketch, "E739", {"start": v(-11.31, -8.14) * mm, "end": v(-11.31, -3.37) * mm});
            skLineSegment(sketch, "E740", {"start": v(-11.31, -3.37) * mm, "end": v(-12.5, -3.37) * mm});
            skLineSegment(sketch, "E741", {"start": v(-12.5, -3.37) * mm, "end": v(-12.5, -4.96) * mm});
            skLineSegment(sketch, "E742", {"start": v(-12.5, -4.96) * mm, "end": v(-12.9, -4.96) * mm});
            skLineSegment(sketch, "E743", {"start": v(-12.9, -4.96) * mm, "end": v(-12.9, -2.98) * mm});
            skLineSegment(sketch, "E744", {"start": v(-12.9, -2.98) * mm, "end": v(-11.31, -2.98) * mm});
            skLineSegment(sketch, "E745", {"start": v(-11.31, -2.98) * mm, "end": v(-11.31, -1.79) * mm});
            skLineSegment(sketch, "E746", {"start": v(-11.31, -1.79) * mm, "end": v(-15.68, -1.79) * mm});
            skLineSegment(sketch, "E747", {"start": v(-15.68, -1.79) * mm, "end": v(-15.68, -2.98) * mm});
            skLineSegment(sketch, "E748", {"start": v(-15.68, -2.98) * mm, "end": v(-14.09, -2.98) * mm});
            skLineSegment(sketch, "E749", {"start": v(-14.09, -2.98) * mm, "end": v(-14.09, -8.14) * mm});
            skLineSegment(sketch, "E750", {"start": v(-14.09, -8.14) * mm, "end": v(-19.25, -8.14) * mm});
            skLineSegment(sketch, "E751", {"start": v(-19.25, -8.14) * mm, "end": v(-19.25, -2.98) * mm});
            skLineSegment(sketch, "E752", {"start": v(-19.25, -2.98) * mm, "end": v(-17.66, -2.98) * mm});
            skLineSegment(sketch, "E753", {"start": v(-17.66, -2.98) * mm, "end": v(-17.66, -1.79) * mm});
            skLineSegment(sketch, "E754", {"start": v(-17.66, -1.79) * mm, "end": v(-22.03, -1.79) * mm});
            skLineSegment(sketch, "E755", {"start": v(-22.03, -1.79) * mm, "end": v(-22.03, -2.98) * mm});
            skLineSegment(sketch, "E756", {"start": v(-22.03, -2.98) * mm, "end": v(-20.44, -2.98) * mm});
            skLineSegment(sketch, "E757", {"start": v(-20.44, -2.98) * mm, "end": v(-20.44, -3.37) * mm});
            skLineSegment(sketch, "E758", {"start": v(-20.44, -3.37) * mm, "end": v(-22.03, -3.37) * mm});
            skLineSegment(sketch, "E759", {"start": v(-22.03, -3.37) * mm, "end": v(-22.03, -8.14) * mm});
            skLineSegment(sketch, "E760", {"start": v(-22.03, -8.14) * mm, "end": v(-22.42, -8.14) * mm});
            skLineSegment(sketch, "E761", {"start": v(-22.42, -17.66) * mm, "end": v(-22.42, -9.33) * mm});
            skLineSegment(sketch, "E762", {"start": v(-22.03, -9.33) * mm, "end": v(-22.03, -14.09) * mm});
            skLineSegment(sketch, "E763", {"start": v(-22.03, -14.09) * mm, "end": v(-20.84, -14.09) * mm});
            skLineSegment(sketch, "E764", {"start": v(-20.84, -14.09) * mm, "end": v(-20.84, -4.56) * mm});
            skLineSegment(sketch, "E765", {"start": v(-20.84, -4.56) * mm, "end": v(-20.44, -4.56) * mm});
            skLineSegment(sketch, "E766", {"start": v(-20.44, -4.56) * mm, "end": v(-20.44, -14.49) * mm});
            skLineSegment(sketch, "E767", {"start": v(-20.44, -14.49) * mm, "end": v(-22.03, -14.49) * mm});
            skLineSegment(sketch, "E768", {"start": v(-22.03, -14.49) * mm, "end": v(-22.03, -15.68) * mm});
            skLineSegment(sketch, "E769", {"start": v(-22.03, -15.68) * mm, "end": v(-17.66, -15.68) * mm});
            skLineSegment(sketch, "E770", {"start": v(-17.66, -15.68) * mm, "end": v(-17.66, -14.49) * mm});
            skLineSegment(sketch, "E771", {"start": v(-17.66, -14.49) * mm, "end": v(-19.25, -14.49) * mm});
            skLineSegment(sketch, "E772", {"start": v(-19.25, -14.49) * mm, "end": v(-19.25, -9.33) * mm});
            skLineSegment(sketch, "E773", {"start": v(-19.25, -9.33) * mm, "end": v(-14.09, -9.33) * mm});
            skLineSegment(sketch, "E774", {"start": v(-14.09, -9.33) * mm, "end": v(-14.09, -14.49) * mm});
            skLineSegment(sketch, "E775", {"start": v(-14.09, -14.49) * mm, "end": v(-15.68, -14.49) * mm});
            skLineSegment(sketch, "E776", {"start": v(-15.68, -14.49) * mm, "end": v(-15.68, -15.68) * mm});
            skLineSegment(sketch, "E777", {"start": v(-15.68, -15.68) * mm, "end": v(-12.5, -15.68) * mm});
            skLineSegment(sketch, "E778", {"start": v(-12.5, -15.68) * mm, "end": v(-12.5, -16.07) * mm});
            skLineSegment(sketch, "E779", {"start": v(-12.5, -16.07) * mm, "end": v(-15.68, -16.07) * mm});
            skLineSegment(sketch, "E780", {"start": v(-15.68, -16.07) * mm, "end": v(-15.68, -17.26) * mm});
            skLineSegment(sketch, "E781", {"start": v(-15.68, -17.26) * mm, "end": v(-11.31, -17.26) * mm});
            skLineSegment(sketch, "E782", {"start": v(-11.31, -17.26) * mm, "end": v(-11.31, -14.49) * mm});
            skLineSegment(sketch, "E783", {"start": v(-11.31, -14.49) * mm, "end": v(-12.9, -14.49) * mm});
            skLineSegment(sketch, "E784", {"start": v(-12.9, -14.49) * mm, "end": v(-12.9, -6.15) * mm});
            skLineSegment(sketch, "E785", {"start": v(-12.9, -6.15) * mm, "end": v(-12.5, -6.15) * mm});
            skLineSegment(sketch, "E786", {"start": v(-12.5, -6.15) * mm, "end": v(-12.5, -14.09) * mm});
            skLineSegment(sketch, "E787", {"start": v(-12.5, -14.09) * mm, "end": v(-11.31, -14.09) * mm});
            skLineSegment(sketch, "E788", {"start": v(-11.31, -14.09) * mm, "end": v(-11.31, -9.33) * mm});
            skLineSegment(sketch, "E789", {"start": v(-11.31, -9.33) * mm, "end": v(-10.91, -9.33) * mm});
            skLineSegment(sketch, "E790", {"start": v(-10.91, -9.33) * mm, "end": v(-10.91, -17.66) * mm});
            skLineSegment(sketch, "E791", {"start": v(-10.91, -17.66) * mm, "end": v(-22.42, -17.66) * mm});
            skLineSegment(sketch, "E792", {"start": v(-14.49, -7.74) * mm, "end": v(-14.49, -6.55) * mm});
            skLineSegment(sketch, "E793", {"start": v(-14.49, -6.55) * mm, "end": v(-17.66, -6.55) * mm});
            skLineSegment(sketch, "E794", {"start": v(-17.66, -6.55) * mm, "end": v(-17.66, -6.15) * mm});
            skLineSegment(sketch, "E795", {"start": v(-17.66, -6.15) * mm, "end": v(-14.49, -6.15) * mm});
            skLineSegment(sketch, "E796", {"start": v(-14.49, -6.15) * mm, "end": v(-14.49, -3.37) * mm});
            skLineSegment(sketch, "E797", {"start": v(-14.49, -3.37) * mm, "end": v(-16.07, -3.37) * mm});
            skLineSegment(sketch, "E798", {"start": v(-16.07, -3.37) * mm, "end": v(-16.07, -1.39) * mm});
            skLineSegment(sketch, "E799", {"start": v(-16.07, -1.39) * mm, "end": v(-11.31, -1.39) * mm});
            skLineSegment(sketch, "E800", {"start": v(-11.31, -1.39) * mm, "end": v(-11.31, -0.2) * mm});
            skLineSegment(sketch, "E801", {"start": v(-11.31, -0.2) * mm, "end": v(-22.03, -0.2) * mm});
            skLineSegment(sketch, "E802", {"start": v(-22.03, -0.2) * mm, "end": v(-22.03, -1.39) * mm});
            skLineSegment(sketch, "E803", {"start": v(-22.03, -1.39) * mm, "end": v(-17.26, -1.39) * mm});
            skLineSegment(sketch, "E804", {"start": v(-17.26, -1.39) * mm, "end": v(-17.26, -4.56) * mm});
            skLineSegment(sketch, "E805", {"start": v(-17.26, -4.56) * mm, "end": v(-15.68, -4.56) * mm});
            skLineSegment(sketch, "E806", {"start": v(-15.68, -4.56) * mm, "end": v(-15.68, -4.96) * mm});
            skLineSegment(sketch, "E807", {"start": v(-15.68, -4.96) * mm, "end": v(-17.66, -4.96) * mm});
            skLineSegment(sketch, "E808", {"start": v(-17.66, -4.96) * mm, "end": v(-17.66, -3.37) * mm});
            skLineSegment(sketch, "E809", {"start": v(-17.66, -3.37) * mm, "end": v(-18.85, -3.37) * mm});
            skLineSegment(sketch, "E810", {"start": v(-18.85, -3.37) * mm, "end": v(-18.85, -7.74) * mm});
            skLineSegment(sketch, "E811", {"start": v(-18.85, -7.74) * mm, "end": v(-14.49, -7.74) * mm});
            skLineSegment(sketch, "E812", {"start": v(-16.07, -17.26) * mm, "end": v(-16.07, -10.91) * mm});
            skLineSegment(sketch, "E813", {"start": v(-16.07, -10.91) * mm, "end": v(-15.68, -10.91) * mm});
            skLineSegment(sketch, "E814", {"start": v(-15.68, -10.91) * mm, "end": v(-15.68, -14.09) * mm});
            skLineSegment(sketch, "E815", {"start": v(-15.68, -14.09) * mm, "end": v(-14.49, -14.09) * mm});
            skLineSegment(sketch, "E816", {"start": v(-14.49, -14.09) * mm, "end": v(-14.49, -9.72) * mm});
            skLineSegment(sketch, "E817", {"start": v(-14.49, -9.72) * mm, "end": v(-18.85, -9.72) * mm});
            skLineSegment(sketch, "E818", {"start": v(-18.85, -9.72) * mm, "end": v(-18.85, -10.91) * mm});
            skLineSegment(sketch, "E819", {"start": v(-18.85, -10.91) * mm, "end": v(-17.26, -10.91) * mm});
            skLineSegment(sketch, "E820", {"start": v(-17.26, -10.91) * mm, "end": v(-17.26, -12.9) * mm});
            skLineSegment(sketch, "E821", {"start": v(-17.26, -12.9) * mm, "end": v(-17.66, -12.9) * mm});
            skLineSegment(sketch, "E822", {"start": v(-17.66, -12.9) * mm, "end": v(-17.66, -11.31) * mm});
            skLineSegment(sketch, "E823", {"start": v(-17.66, -11.31) * mm, "end": v(-18.85, -11.31) * mm});
            skLineSegment(sketch, "E824", {"start": v(-18.85, -11.31) * mm, "end": v(-18.85, -14.09) * mm});
            skLineSegment(sketch, "E825", {"start": v(-18.85, -14.09) * mm, "end": v(-17.26, -14.09) * mm});
            skLineSegment(sketch, "E826", {"start": v(-17.26, -14.09) * mm, "end": v(-17.26, -16.07) * mm});
            skLineSegment(sketch, "E827", {"start": v(-17.26, -16.07) * mm, "end": v(-22.03, -16.07) * mm});
            skLineSegment(sketch, "E828", {"start": v(-22.03, -16.07) * mm, "end": v(-22.03, -17.26) * mm});
            skLineSegment(sketch, "E829", {"start": v(-22.03, -17.26) * mm, "end": v(-16.07, -17.26) * mm});
            skLineSegment(sketch, "E830", {"start": v(-9.72, -12.9) * mm, "end": v(-9.72, -3.37) * mm});
            skLineSegment(sketch, "E831", {"start": v(-9.72, -3.37) * mm, "end": v(-10.91, -3.37) * mm});
            skLineSegment(sketch, "E832", {"start": v(-10.91, -3.37) * mm, "end": v(-10.91, -8.14) * mm});
            skLineSegment(sketch, "E833", {"start": v(-11.31, -8.14) * mm, "end": v(-11.31, 0.2) * mm});
            skLineSegment(sketch, "E834", {"start": v(-11.31, 0.2) * mm, "end": v(0.2, 0.2) * mm});
            skLineSegment(sketch, "E835", {"start": v(0.2, 0.2) * mm, "end": v(0.2, -8.14) * mm});
            skLineSegment(sketch, "E836", {"start": v(0.2, -8.14) * mm, "end": v(-0.2, -8.14) * mm});
            skLineSegment(sketch, "E837", {"start": v(-0.2, -8.14) * mm, "end": v(-0.2, -0.2) * mm});
            skLineSegment(sketch, "E838", {"start": v(-0.2, -0.2) * mm, "end": v(-1.39, -0.2) * mm});
            skLineSegment(sketch, "E839", {"start": v(-1.39, -0.2) * mm, "end": v(-1.39, -1.79) * mm});
            skLineSegment(sketch, "E840", {"start": v(-1.39, -1.79) * mm, "end": v(-1.79, -1.79) * mm});
            skLineSegment(sketch, "E841", {"start": v(-1.79, -1.79) * mm, "end": v(-1.79, -0.2) * mm});
            skLineSegment(sketch, "E842", {"start": v(-1.79, -0.2) * mm, "end": v(-10.91, -0.2) * mm});
            skLineSegment(sketch, "E843", {"start": v(-10.91, -0.2) * mm, "end": v(-10.91, -1.39) * mm});
            skLineSegment(sketch, "E844", {"start": v(-10.91, -1.39) * mm, "end": v(-6.15, -1.39) * mm});
            skLineSegment(sketch, "E845", {"start": v(-6.15, -1.39) * mm, "end": v(-6.15, -1.79) * mm});
            skLineSegment(sketch, "E846", {"start": v(-6.15, -1.79) * mm, "end": v(-10.91, -1.79) * mm});
            skLineSegment(sketch, "E847", {"start": v(-10.91, -1.79) * mm, "end": v(-10.91, -2.98) * mm});
            skLineSegment(sketch, "E848", {"start": v(-10.91, -2.98) * mm, "end": v(-9.33, -2.98) * mm});
            skLineSegment(sketch, "E849", {"start": v(-9.33, -2.98) * mm, "end": v(-9.33, -12.9) * mm});
            skLineSegment(sketch, "E850", {"start": v(-9.33, -12.9) * mm, "end": v(-9.72, -12.9) * mm});
            skLineSegment(sketch, "E851", {"start": v(-11.31, -17.66) * mm, "end": v(-11.31, -9.33) * mm});
            skLineSegment(sketch, "E852", {"start": v(-10.91, -9.33) * mm, "end": v(-10.91, -14.09) * mm});
            skLineSegment(sketch, "E853", {"start": v(-10.91, -14.09) * mm, "end": v(-9.33, -14.09) * mm});
            skLineSegment(sketch, "E854", {"start": v(-9.33, -14.09) * mm, "end": v(-9.33, -14.49) * mm});
            skLineSegment(sketch, "E855", {"start": v(-9.33, -14.49) * mm, "end": v(-10.91, -14.49) * mm});
            skLineSegment(sketch, "E856", {"start": v(-10.91, -14.49) * mm, "end": v(-10.91, -17.26) * mm});
            skLineSegment(sketch, "E857", {"start": v(-10.91, -17.26) * mm, "end": v(-6.55, -17.26) * mm});
            skLineSegment(sketch, "E858", {"start": v(-6.55, -17.26) * mm, "end": v(-6.55, -16.07) * mm});
            skLineSegment(sketch, "E859", {"start": v(-6.55, -16.07) * mm, "end": v(-9.72, -16.07) * mm});
            skLineSegment(sketch, "E860", {"start": v(-9.72, -16.07) * mm, "end": v(-9.72, -15.68) * mm});
            skLineSegment(sketch, "E861", {"start": v(-9.72, -15.68) * mm, "end": v(-6.55, -15.68) * mm});
            skLineSegment(sketch, "E862", {"start": v(-6.55, -15.68) * mm, "end": v(-6.55, -14.49) * mm});
            skLineSegment(sketch, "E863", {"start": v(-6.55, -14.49) * mm, "end": v(-8.14, -14.49) * mm});
            skLineSegment(sketch, "E864", {"start": v(-8.14, -14.49) * mm, "end": v(-8.14, -9.33) * mm});
            skLineSegment(sketch, "E865", {"start": v(-8.14, -9.33) * mm, "end": v(-4.56, -9.33) * mm});
            skLineSegment(sketch, "E866", {"start": v(-4.56, -9.33) * mm, "end": v(-4.56, -10.91) * mm});
            skLineSegment(sketch, "E867", {"start": v(-4.56, -10.91) * mm, "end": v(-2.98, -10.91) * mm});
            skLineSegment(sketch, "E868", {"start": v(-2.98, -10.91) * mm, "end": v(-2.98, -14.49) * mm});
            skLineSegment(sketch, "E869", {"start": v(-2.98, -14.49) * mm, "end": v(-4.56, -14.49) * mm});
            skLineSegment(sketch, "E870", {"start": v(-4.56, -14.49) * mm, "end": v(-4.56, -15.68) * mm});
            skLineSegment(sketch, "E871", {"start": v(-4.56, -15.68) * mm, "end": v(-0.2, -15.68) * mm});
            skLineSegment(sketch, "E872", {"start": v(-0.2, -15.68) * mm, "end": v(-0.2, -14.49) * mm});
            skLineSegment(sketch, "E873", {"start": v(-0.2, -14.49) * mm, "end": v(-1.79, -14.49) * mm});
            skLineSegment(sketch, "E874", {"start": v(-1.79, -14.49) * mm, "end": v(-1.79, -9.72) * mm});
            skLineSegment(sketch, "E875", {"start": v(-1.79, -9.72) * mm, "end": v(-3.37, -9.72) * mm});
            skLineSegment(sketch, "E876", {"start": v(-3.37, -9.72) * mm, "end": v(-3.37, -7.74) * mm});
            skLineSegment(sketch, "E877", {"start": v(-3.37, -7.74) * mm, "end": v(-1.79, -7.74) * mm});
            skLineSegment(sketch, "E878", {"start": v(-1.79, -7.74) * mm, "end": v(-1.79, -3.37) * mm});
            skLineSegment(sketch, "E879", {"start": v(-1.79, -3.37) * mm, "end": v(-3.37, -3.37) * mm});
            skLineSegment(sketch, "E880", {"start": v(-3.37, -3.37) * mm, "end": v(-3.37, -1.79) * mm});
            skLineSegment(sketch, "E881", {"start": v(-3.37, -1.79) * mm, "end": v(-4.96, -1.79) * mm});
            skLineSegment(sketch, "E882", {"start": v(-4.96, -1.79) * mm, "end": v(-4.96, -1.39) * mm});
            skLineSegment(sketch, "E883", {"start": v(-4.96, -1.39) * mm, "end": v(-2.98, -1.39) * mm});
            skLineSegment(sketch, "E884", {"start": v(-2.98, -1.39) * mm, "end": v(-2.98, -2.98) * mm});
            skLineSegment(sketch, "E885", {"start": v(-2.98, -2.98) * mm, "end": v(-1.39, -2.98) * mm});
            skLineSegment(sketch, "E886", {"start": v(-1.39, -2.98) * mm, "end": v(-1.39, -8.14) * mm});
            skLineSegment(sketch, "E887", {"start": v(-1.39, -8.14) * mm, "end": v(-2.98, -8.14) * mm});
            skLineSegment(sketch, "E888", {"start": v(-2.98, -8.14) * mm, "end": v(-2.98, -9.33) * mm});
            skLineSegment(sketch, "E889", {"start": v(-2.98, -9.33) * mm, "end": v(-1.39, -9.33) * mm});
            skLineSegment(sketch, "E890", {"start": v(-1.39, -9.33) * mm, "end": v(-1.39, -14.09) * mm});
            skLineSegment(sketch, "E891", {"start": v(-1.39, -14.09) * mm, "end": v(-0.2, -14.09) * mm});
            skLineSegment(sketch, "E892", {"start": v(-0.2, -14.09) * mm, "end": v(-0.2, -9.33) * mm});
            skLineSegment(sketch, "E893", {"start": v(-0.2, -9.33) * mm, "end": v(0.2, -9.33) * mm});
            skLineSegment(sketch, "E894", {"start": v(0.2, -9.33) * mm, "end": v(0.2, -17.66) * mm});
            skLineSegment(sketch, "E895", {"start": v(0.2, -17.66) * mm, "end": v(-11.31, -17.66) * mm});
            skLineSegment(sketch, "E896", {"start": v(-8.14, -8.14) * mm, "end": v(-8.14, -7.74) * mm});
            skLineSegment(sketch, "E897", {"start": v(-8.14, -7.74) * mm, "end": v(-4.96, -7.74) * mm});
            skLineSegment(sketch, "E898", {"start": v(-4.96, -7.74) * mm, "end": v(-4.96, -6.15) * mm});
            skLineSegment(sketch, "E899", {"start": v(-4.96, -6.15) * mm, "end": v(-3.37, -6.15) * mm});
            skLineSegment(sketch, "E900", {"start": v(-3.37, -6.15) * mm, "end": v(-3.37, -4.96) * mm});
            skLineSegment(sketch, "E901", {"start": v(-3.37, -4.96) * mm, "end": v(-4.96, -4.96) * mm});
            skLineSegment(sketch, "E902", {"start": v(-4.96, -4.96) * mm, "end": v(-4.96, -3.37) * mm});
            skLineSegment(sketch, "E903", {"start": v(-4.96, -3.37) * mm, "end": v(-7.74, -3.37) * mm});
            skLineSegment(sketch, "E904", {"start": v(-7.74, -3.37) * mm, "end": v(-7.74, -4.56) * mm});
            skLineSegment(sketch, "E905", {"start": v(-7.74, -4.56) * mm, "end": v(-6.15, -4.56) * mm});
            skLineSegment(sketch, "E906", {"start": v(-6.15, -4.56) * mm, "end": v(-6.15, -6.55) * mm});
            skLineSegment(sketch, "E907", {"start": v(-6.15, -6.55) * mm, "end": v(-6.55, -6.55) * mm});
            skLineSegment(sketch, "E908", {"start": v(-6.55, -6.55) * mm, "end": v(-6.55, -4.96) * mm});
            skLineSegment(sketch, "E909", {"start": v(-6.55, -4.96) * mm, "end": v(-7.74, -4.96) * mm});
            skLineSegment(sketch, "E910", {"start": v(-7.74, -4.96) * mm, "end": v(-7.74, -6.55) * mm});
            skLineSegment(sketch, "E911", {"start": v(-7.74, -6.55) * mm, "end": v(-8.14, -6.55) * mm});
            skLineSegment(sketch, "E912", {"start": v(-8.14, -6.55) * mm, "end": v(-8.14, -2.98) * mm});
            skLineSegment(sketch, "E913", {"start": v(-8.14, -2.98) * mm, "end": v(-4.56, -2.98) * mm});
            skLineSegment(sketch, "E914", {"start": v(-4.56, -2.98) * mm, "end": v(-4.56, -4.56) * mm});
            skLineSegment(sketch, "E915", {"start": v(-4.56, -4.56) * mm, "end": v(-2.98, -4.56) * mm});
            skLineSegment(sketch, "E916", {"start": v(-2.98, -4.56) * mm, "end": v(-2.98, -6.55) * mm});
            skLineSegment(sketch, "E917", {"start": v(-2.98, -6.55) * mm, "end": v(-4.56, -6.55) * mm});
            skLineSegment(sketch, "E918", {"start": v(-4.56, -6.55) * mm, "end": v(-4.56, -8.14) * mm});
            skLineSegment(sketch, "E919", {"start": v(-4.56, -8.14) * mm, "end": v(-8.14, -8.14) * mm});
            skLineSegment(sketch, "E920", {"start": v(-0.2, -17.26) * mm, "end": v(-0.2, -16.07) * mm});
            skLineSegment(sketch, "E921", {"start": v(-0.2, -16.07) * mm, "end": v(-4.96, -16.07) * mm});
            skLineSegment(sketch, "E922", {"start": v(-4.96, -16.07) * mm, "end": v(-4.96, -14.09) * mm});
            skLineSegment(sketch, "E923", {"start": v(-4.96, -14.09) * mm, "end": v(-3.37, -14.09) * mm});
            skLineSegment(sketch, "E924", {"start": v(-3.37, -14.09) * mm, "end": v(-3.37, -11.31) * mm});
            skLineSegment(sketch, "E925", {"start": v(-3.37, -11.31) * mm, "end": v(-4.96, -11.31) * mm});
            skLineSegment(sketch, "E926", {"start": v(-4.96, -11.31) * mm, "end": v(-4.96, -9.72) * mm});
            skLineSegment(sketch, "E927", {"start": v(-4.96, -9.72) * mm, "end": v(-7.74, -9.72) * mm});
            skLineSegment(sketch, "E928", {"start": v(-7.74, -9.72) * mm, "end": v(-7.74, -12.5) * mm});
            skLineSegment(sketch, "E929", {"start": v(-7.74, -12.5) * mm, "end": v(-6.55, -12.5) * mm});
            skLineSegment(sketch, "E930", {"start": v(-6.55, -12.5) * mm, "end": v(-6.55, -10.91) * mm});
            skLineSegment(sketch, "E931", {"start": v(-6.55, -10.91) * mm, "end": v(-6.15, -10.91) * mm});
            skLineSegment(sketch, "E932", {"start": v(-6.15, -10.91) * mm, "end": v(-6.15, -12.5) * mm});
            skLineSegment(sketch, "E933", {"start": v(-6.15, -12.5) * mm, "end": v(-4.56, -12.5) * mm});
            skLineSegment(sketch, "E934", {"start": v(-4.56, -12.5) * mm, "end": v(-4.56, -12.9) * mm});
            skLineSegment(sketch, "E935", {"start": v(-4.56, -12.9) * mm, "end": v(-7.74, -12.9) * mm});
            skLineSegment(sketch, "E936", {"start": v(-7.74, -12.9) * mm, "end": v(-7.74, -14.09) * mm});
            skLineSegment(sketch, "E937", {"start": v(-7.74, -14.09) * mm, "end": v(-6.15, -14.09) * mm});
            skLineSegment(sketch, "E938", {"start": v(-6.15, -14.09) * mm, "end": v(-6.15, -17.26) * mm});
            skLineSegment(sketch, "E939", {"start": v(-6.15, -17.26) * mm, "end": v(-0.2, -17.26) * mm});
            skLineSegment(sketch, "E940", {"start": v(4.56, -16.07) * mm, "end": v(4.56, -15.68) * mm});
            skLineSegment(sketch, "E941", {"start": v(4.56, -15.68) * mm, "end": v(9.33, -15.68) * mm});
            skLineSegment(sketch, "E942", {"start": v(9.33, -15.68) * mm, "end": v(9.33, -12.9) * mm});
            skLineSegment(sketch, "E943", {"start": v(9.33, -12.9) * mm, "end": v(8.14, -12.9) * mm});
            skLineSegment(sketch, "E944", {"start": v(8.14, -12.9) * mm, "end": v(8.14, -14.49) * mm});
            skLineSegment(sketch, "E945", {"start": v(8.14, -14.49) * mm, "end": v(2.98, -14.49) * mm});
            skLineSegment(sketch, "E946", {"start": v(2.98, -14.49) * mm, "end": v(2.98, -9.33) * mm});
            skLineSegment(sketch, "E947", {"start": v(2.98, -9.33) * mm, "end": v(6.55, -9.33) * mm});
            skLineSegment(sketch, "E948", {"start": v(6.55, -9.33) * mm, "end": v(6.55, -10.91) * mm});
            skLineSegment(sketch, "E949", {"start": v(6.55, -10.91) * mm, "end": v(7.74, -10.91) * mm});
            skLineSegment(sketch, "E950", {"start": v(7.74, -10.91) * mm, "end": v(7.74, -6.55) * mm});
            skLineSegment(sketch, "E951", {"start": v(7.74, -6.55) * mm, "end": v(6.55, -6.55) * mm});
            skLineSegment(sketch, "E952", {"start": v(6.55, -6.55) * mm, "end": v(6.55, -8.14) * mm});
            skLineSegment(sketch, "E953", {"start": v(6.55, -8.14) * mm, "end": v(2.98, -8.14) * mm});
            skLineSegment(sketch, "E954", {"start": v(2.98, -8.14) * mm, "end": v(2.98, -2.98) * mm});
            skLineSegment(sketch, "E955", {"start": v(2.98, -2.98) * mm, "end": v(8.14, -2.98) * mm});
            skLineSegment(sketch, "E956", {"start": v(8.14, -2.98) * mm, "end": v(8.14, -4.56) * mm});
            skLineSegment(sketch, "E957", {"start": v(8.14, -4.56) * mm, "end": v(9.33, -4.56) * mm});
            skLineSegment(sketch, "E958", {"start": v(9.33, -4.56) * mm, "end": v(9.33, -1.79) * mm});
            skLineSegment(sketch, "E959", {"start": v(9.33, -1.79) * mm, "end": v(0.2, -1.79) * mm});
            skLineSegment(sketch, "E960", {"start": v(0.2, -1.79) * mm, "end": v(0.2, -2.98) * mm});
            skLineSegment(sketch, "E961", {"start": v(0.2, -2.98) * mm, "end": v(1.79, -2.98) * mm});
            skLineSegment(sketch, "E962", {"start": v(1.79, -2.98) * mm, "end": v(1.79, -3.37) * mm});
            skLineSegment(sketch, "E963", {"start": v(1.79, -3.37) * mm, "end": v(0.2, -3.37) * mm});
            skLineSegment(sketch, "E964", {"start": v(0.2, -3.37) * mm, "end": v(0.2, -8.14) * mm});
            skLineSegment(sketch, "E965", {"start": v(-0.2, -8.14) * mm, "end": v(-0.2, 0.2) * mm});
            skLineSegment(sketch, "E966", {"start": v(-0.2, 0.2) * mm, "end": v(9.67, 0.2) * mm});
            skLineSegment(sketch, "E967", {"start": v(11.31, 0.2) * mm, "end": v(11.31, -8.14) * mm});
            skLineSegment(sketch, "E968", {"start": v(11.31, -8.14) * mm, "end": v(9.72, -8.14) * mm});
            skLineSegment(sketch, "E969", {"start": v(9.72, -8.14) * mm, "end": v(9.72, -9.72) * mm});
            skLineSegment(sketch, "E970", {"start": v(9.72, -9.72) * mm, "end": v(9.33, -9.72) * mm});
            skLineSegment(sketch, "E971", {"start": v(9.33, -9.72) * mm, "end": v(9.33, -7.74) * mm});
            skLineSegment(sketch, "E972", {"start": v(9.33, -7.74) * mm, "end": v(10.91, -7.74) * mm});
            skLineSegment(sketch, "E973", {"start": v(10.91, -7.74) * mm, "end": v(10.91, -0.2) * mm});
            skLineSegment(sketch, "E974", {"start": v(8.14, -1.39) * mm, "end": v(9.72, -1.39) * mm});
            skLineSegment(sketch, "E975", {"start": v(9.72, -1.39) * mm, "end": v(9.72, -6.55) * mm});
            skLineSegment(sketch, "E976", {"start": v(9.72, -6.55) * mm, "end": v(9.33, -6.55) * mm});
            skLineSegment(sketch, "E977", {"start": v(9.33, -6.55) * mm, "end": v(9.33, -4.96) * mm});
            skLineSegment(sketch, "E978", {"start": v(9.33, -4.96) * mm, "end": v(7.74, -4.96) * mm});
            skLineSegment(sketch, "E979", {"start": v(7.74, -4.96) * mm, "end": v(7.74, -3.37) * mm});
            skLineSegment(sketch, "E980", {"start": v(7.74, -3.37) * mm, "end": v(6.55, -3.37) * mm});
            skLineSegment(sketch, "E981", {"start": v(6.55, -3.37) * mm, "end": v(6.55, -4.96) * mm});
            skLineSegment(sketch, "E982", {"start": v(6.55, -4.96) * mm, "end": v(6.15, -4.96) * mm});
            skLineSegment(sketch, "E983", {"start": v(6.15, -4.96) * mm, "end": v(6.15, -3.37) * mm});
            skLineSegment(sketch, "E984", {"start": v(6.15, -3.37) * mm, "end": v(3.37, -3.37) * mm});
            skLineSegment(sketch, "E985", {"start": v(3.37, -3.37) * mm, "end": v(3.37, -6.15) * mm});
            skLineSegment(sketch, "E986", {"start": v(3.37, -6.15) * mm, "end": v(4.56, -6.15) * mm});
            skLineSegment(sketch, "E987", {"start": v(4.56, -6.15) * mm, "end": v(4.56, -4.56) * mm});
            skLineSegment(sketch, "E988", {"start": v(4.56, -4.56) * mm, "end": v(4.96, -4.56) * mm});
            skLineSegment(sketch, "E989", {"start": v(4.96, -4.56) * mm, "end": v(4.96, -6.55) * mm});
            skLineSegment(sketch, "E990", {"start": v(4.96, -6.55) * mm, "end": v(3.37, -6.55) * mm});
            skLineSegment(sketch, "E991", {"start": v(3.37, -6.55) * mm, "end": v(3.37, -7.74) * mm});
            skLineSegment(sketch, "E992", {"start": v(3.37, -7.74) * mm, "end": v(6.15, -7.74) * mm});
            skLineSegment(sketch, "E993", {"start": v(6.15, -7.74) * mm, "end": v(6.15, -6.15) * mm});
            skLineSegment(sketch, "E994", {"start": v(6.15, -6.15) * mm, "end": v(8.14, -6.15) * mm});
            skLineSegment(sketch, "E995", {"start": v(8.14, -6.15) * mm, "end": v(8.14, -11.31) * mm});
            skLineSegment(sketch, "E996", {"start": v(8.14, -11.31) * mm, "end": v(4.56, -11.31) * mm});
            skLineSegment(sketch, "E997", {"start": v(4.56, -11.31) * mm, "end": v(4.56, -10.91) * mm});
            skLineSegment(sketch, "E998", {"start": v(4.56, -10.91) * mm, "end": v(6.15, -10.91) * mm});
            skLineSegment(sketch, "E999", {"start": v(6.15, -10.91) * mm, "end": v(6.15, -9.72) * mm});
            skLineSegment(sketch, "E1000", {"start": v(6.15, -9.72) * mm, "end": v(3.37, -9.72) * mm});
            skLineSegment(sketch, "E1001", {"start": v(3.37, -9.72) * mm, "end": v(3.37, -12.5) * mm});
            skLineSegment(sketch, "E1002", {"start": v(3.37, -12.5) * mm, "end": v(6.55, -12.5) * mm});
            skLineSegment(sketch, "E1003", {"start": v(6.55, -12.5) * mm, "end": v(6.55, -12.9) * mm});
            skLineSegment(sketch, "E1004", {"start": v(6.55, -12.9) * mm, "end": v(3.37, -12.9) * mm});
            skLineSegment(sketch, "E1005", {"start": v(3.37, -12.9) * mm, "end": v(3.37, -14.09) * mm});
            skLineSegment(sketch, "E1006", {"start": v(3.37, -14.09) * mm, "end": v(7.74, -14.09) * mm});
            skLineSegment(sketch, "E1007", {"start": v(7.74, -14.09) * mm, "end": v(7.74, -12.5) * mm});
            skLineSegment(sketch, "E1008", {"start": v(7.74, -12.5) * mm, "end": v(9.72, -12.5) * mm});
            skLineSegment(sketch, "E1009", {"start": v(9.72, -12.5) * mm, "end": v(9.72, -16.07) * mm});
            skLineSegment(sketch, "E1010", {"start": v(9.72, -16.07) * mm, "end": v(4.56, -16.07) * mm});
            skLineSegment(sketch, "E1011", {"start": v(-0.2, -17.66) * mm, "end": v(-0.2, -9.33) * mm});
            skLineSegment(sketch, "E1012", {"start": v(0.2, -9.33) * mm, "end": v(0.2, -14.09) * mm});
            skLineSegment(sketch, "E1013", {"start": v(0.2, -14.09) * mm, "end": v(1.39, -14.09) * mm});
            skLineSegment(sketch, "E1014", {"start": v(1.39, -14.09) * mm, "end": v(1.39, -4.56) * mm});
            skLineSegment(sketch, "E1015", {"start": v(1.39, -4.56) * mm, "end": v(1.79, -4.56) * mm});
            skLineSegment(sketch, "E1016", {"start": v(1.79, -4.56) * mm, "end": v(1.79, -14.49) * mm});
            skLineSegment(sketch, "E1017", {"start": v(1.79, -14.49) * mm, "end": v(0.2, -14.49) * mm});
            skLineSegment(sketch, "E1018", {"start": v(0.2, -14.49) * mm, "end": v(0.2, -15.68) * mm});
            skLineSegment(sketch, "E1019", {"start": v(0.2, -15.68) * mm, "end": v(3.37, -15.68) * mm});
            skLineSegment(sketch, "E1020", {"start": v(3.37, -15.68) * mm, "end": v(3.37, -16.07) * mm});
            skLineSegment(sketch, "E1021", {"start": v(3.37, -16.07) * mm, "end": v(0.2, -16.07) * mm});
            skLineSegment(sketch, "E1022", {"start": v(0.2, -16.07) * mm, "end": v(0.2, -17.26) * mm});
            skLineSegment(sketch, "E1023", {"start": v(0.2, -17.26) * mm, "end": v(10.91, -17.26) * mm});
            skLineSegment(sketch, "E1024", {"start": v(10.91, -17.26) * mm, "end": v(10.91, -11.31) * mm});
            skLineSegment(sketch, "E1025", {"start": v(10.91, -11.31) * mm, "end": v(9.33, -11.31) * mm});
            skLineSegment(sketch, "E1026", {"start": v(9.33, -11.31) * mm, "end": v(9.33, -10.91) * mm});
            skLineSegment(sketch, "E1027", {"start": v(9.33, -10.91) * mm, "end": v(10.91, -10.91) * mm});
            skLineSegment(sketch, "E1028", {"start": v(10.91, -10.91) * mm, "end": v(10.91, -9.33) * mm});
            skLineSegment(sketch, "E1029", {"start": v(10.91, -9.33) * mm, "end": v(11.31, -9.33) * mm});
            skLineSegment(sketch, "E1030", {"start": v(11.31, -9.33) * mm, "end": v(11.31, -17.66) * mm});
            skLineSegment(sketch, "E1031", {"start": v(11.31, -17.66) * mm, "end": v(-0.2, -17.66) * mm});
            skLineSegment(sketch, "E1032", {"start": v(7.74, -0.2) * mm, "end": v(0.2, -0.2) * mm});
            skLineSegment(sketch, "E1033", {"start": v(0.2, -0.2) * mm, "end": v(0.2, -1.39) * mm});
            skLineSegment(sketch, "E1034", {"start": v(0.2, -1.39) * mm, "end": v(7.74, -1.39) * mm});
            skLineSegment(sketch, "E1035", {"start": v(20.44, -12.9) * mm, "end": v(20.44, -1.79) * mm});
            skLineSegment(sketch, "E1036", {"start": v(20.44, -1.79) * mm, "end": v(16.07, -1.79) * mm});
            skLineSegment(sketch, "E1037", {"start": v(16.07, -1.79) * mm, "end": v(16.07, -3.37) * mm});
            skLineSegment(sketch, "E1038", {"start": v(16.07, -3.37) * mm, "end": v(15.68, -3.37) * mm});
            skLineSegment(sketch, "E1039", {"start": v(15.68, -3.37) * mm, "end": v(15.68, -1.39) * mm});
            skLineSegment(sketch, "E1040", {"start": v(15.68, -1.39) * mm, "end": v(20.44, -1.39) * mm});
            skLineSegment(sketch, "E1041", {"start": v(20.44, -1.39) * mm, "end": v(20.44, -0.2) * mm});
            skLineSegment(sketch, "E1042", {"start": v(20.44, -0.2) * mm, "end": v(14.49, -0.2) * mm});
            skLineSegment(sketch, "E1043", {"start": v(14.49, -0.2) * mm, "end": v(14.49, -1.79) * mm});
            skLineSegment(sketch, "E1044", {"start": v(14.49, -1.79) * mm, "end": v(14.09, -1.79) * mm});
            skLineSegment(sketch, "E1045", {"start": v(14.09, -1.79) * mm, "end": v(14.09, -0.2) * mm});
            skLineSegment(sketch, "E1046", {"start": v(14.09, -0.2) * mm, "end": v(11.31, -0.2) * mm});
            skLineSegment(sketch, "E1047", {"start": v(11.31, -0.2) * mm, "end": v(11.31, -2.98) * mm});
            skLineSegment(sketch, "E1048", {"start": v(11.31, -2.98) * mm, "end": v(12.5, -2.98) * mm});
            skLineSegment(sketch, "E1049", {"start": v(12.5, -2.98) * mm, "end": v(12.5, -1.39) * mm});
            skLineSegment(sketch, "E1050", {"start": v(12.5, -1.39) * mm, "end": v(12.9, -1.39) * mm});
            skLineSegment(sketch, "E1051", {"start": v(12.9, -1.39) * mm, "end": v(12.9, -3.37) * mm});
            skLineSegment(sketch, "E1052", {"start": v(12.9, -3.37) * mm, "end": v(11.31, -3.37) * mm});
            skLineSegment(sketch, "E1053", {"start": v(11.31, -3.37) * mm, "end": v(11.31, -8.14) * mm});
            skLineSegment(sketch, "E1054", {"start": v(11.31, -8.14) * mm, "end": v(10.91, -8.14) * mm});
            skLineSegment(sketch, "E1055", {"start": v(10.91, -8.14) * mm, "end": v(10.91, 0.2) * mm});
            skLineSegment(sketch, "E1056", {"start": v(10.91, 0.2) * mm, "end": v(22.42, 0.2) * mm});
            skLineSegment(sketch, "E1057", {"start": v(22.42, 0.2) * mm, "end": v(22.42, -8.14) * mm});
            skLineSegment(sketch, "E1058", {"start": v(22.42, -8.14) * mm, "end": v(22.03, -8.14) * mm});
            skLineSegment(sketch, "E1059", {"start": v(22.03, -8.14) * mm, "end": v(22.03, -0.2) * mm});
            skLineSegment(sketch, "E1060", {"start": v(22.03, -0.2) * mm, "end": v(20.84, -0.2) * mm});
            skLineSegment(sketch, "E1061", {"start": v(20.84, -0.2) * mm, "end": v(20.84, -12.9) * mm});
            skLineSegment(sketch, "E1062", {"start": v(20.84, -12.9) * mm, "end": v(20.44, -12.9) * mm});
            skLineSegment(sketch, "E1063", {"start": v(10.91, -17.66) * mm, "end": v(10.91, -9.33) * mm});
            skLineSegment(sketch, "E1064", {"start": v(11.31, -9.33) * mm, "end": v(11.31, -14.09) * mm});
            skLineSegment(sketch, "E1065", {"start": v(11.31, -14.09) * mm, "end": v(12.5, -14.09) * mm});
            skLineSegment(sketch, "E1066", {"start": v(12.5, -14.09) * mm, "end": v(12.5, -4.56) * mm});
            skLineSegment(sketch, "E1067", {"start": v(12.5, -4.56) * mm, "end": v(14.09, -4.56) * mm});
            skLineSegment(sketch, "E1068", {"start": v(14.09, -4.56) * mm, "end": v(14.09, -2.98) * mm});
            skLineSegment(sketch, "E1069", {"start": v(14.09, -2.98) * mm, "end": v(14.49, -2.98) * mm});
            skLineSegment(sketch, "E1070", {"start": v(14.49, -2.98) * mm, "end": v(14.49, -4.96) * mm});
            skLineSegment(sketch, "E1071", {"start": v(14.49, -4.96) * mm, "end": v(12.9, -4.96) * mm});
            skLineSegment(sketch, "E1072", {"start": v(12.9, -4.96) * mm, "end": v(12.9, -14.49) * mm});
            skLineSegment(sketch, "E1073", {"start": v(12.9, -14.49) * mm, "end": v(11.31, -14.49) * mm});
            skLineSegment(sketch, "E1074", {"start": v(11.31, -14.49) * mm, "end": v(11.31, -15.68) * mm});
            skLineSegment(sketch, "E1075", {"start": v(11.31, -15.68) * mm, "end": v(15.68, -15.68) * mm});
            skLineSegment(sketch, "E1076", {"start": v(15.68, -15.68) * mm, "end": v(15.68, -14.49) * mm});
            skLineSegment(sketch, "E1077", {"start": v(15.68, -14.49) * mm, "end": v(14.09, -14.49) * mm});
            skLineSegment(sketch, "E1078", {"start": v(14.09, -14.49) * mm, "end": v(14.09, -10.91) * mm});
            skLineSegment(sketch, "E1079", {"start": v(14.09, -10.91) * mm, "end": v(19.25, -10.91) * mm});
            skLineSegment(sketch, "E1080", {"start": v(19.25, -10.91) * mm, "end": v(19.25, -14.49) * mm});
            skLineSegment(sketch, "E1081", {"start": v(19.25, -14.49) * mm, "end": v(17.66, -14.49) * mm});
            skLineSegment(sketch, "E1082", {"start": v(17.66, -14.49) * mm, "end": v(17.66, -15.68) * mm});
            skLineSegment(sketch, "E1083", {"start": v(17.66, -15.68) * mm, "end": v(20.84, -15.68) * mm});
            skLineSegment(sketch, "E1084", {"start": v(20.84, -15.68) * mm, "end": v(20.84, -16.07) * mm});
            skLineSegment(sketch, "E1085", {"start": v(20.84, -16.07) * mm, "end": v(19.25, -16.07) * mm});
            skLineSegment(sketch, "E1086", {"start": v(19.25, -16.07) * mm, "end": v(19.25, -17.26) * mm});
            skLineSegment(sketch, "E1087", {"start": v(19.25, -17.26) * mm, "end": v(22.03, -17.26) * mm});
            skLineSegment(sketch, "E1088", {"start": v(22.03, -17.26) * mm, "end": v(22.03, -14.49) * mm});
            skLineSegment(sketch, "E1089", {"start": v(22.03, -14.49) * mm, "end": v(20.44, -14.49) * mm});
            skLineSegment(sketch, "E1090", {"start": v(20.44, -14.49) * mm, "end": v(20.44, -14.09) * mm});
            skLineSegment(sketch, "E1091", {"start": v(20.44, -14.09) * mm, "end": v(22.03, -14.09) * mm});
            skLineSegment(sketch, "E1092", {"start": v(22.03, -14.09) * mm, "end": v(22.03, -9.72) * mm});
            skLineSegment(sketch, "E1093", {"start": v(22.03, -9.72) * mm, "end": v(22.42, -9.72) * mm});
            skLineSegment(sketch, "E1094", {"start": v(22.42, -9.72) * mm, "end": v(22.42, -17.66) * mm});
            skLineSegment(sketch, "E1095", {"start": v(22.42, -17.66) * mm, "end": v(10.91, -17.66) * mm});
            skLineSegment(sketch, "E1096", {"start": v(18.85, -17.26) * mm, "end": v(18.85, -16.07) * mm});
            skLineSegment(sketch, "E1097", {"start": v(18.85, -16.07) * mm, "end": v(17.26, -16.07) * mm});
            skLineSegment(sketch, "E1098", {"start": v(17.26, -16.07) * mm, "end": v(17.26, -14.09) * mm});
            skLineSegment(sketch, "E1099", {"start": v(17.26, -14.09) * mm, "end": v(18.85, -14.09) * mm});
            skLineSegment(sketch, "E1100", {"start": v(18.85, -14.09) * mm, "end": v(18.85, -11.31) * mm});
            skLineSegment(sketch, "E1101", {"start": v(18.85, -11.31) * mm, "end": v(14.49, -11.31) * mm});
            skLineSegment(sketch, "E1102", {"start": v(14.49, -11.31) * mm, "end": v(14.49, -14.09) * mm});
            skLineSegment(sketch, "E1103", {"start": v(14.49, -14.09) * mm, "end": v(15.68, -14.09) * mm});
            skLineSegment(sketch, "E1104", {"start": v(15.68, -14.09) * mm, "end": v(15.68, -12.5) * mm});
            skLineSegment(sketch, "E1105", {"start": v(15.68, -12.5) * mm, "end": v(17.66, -12.5) * mm});
            skLineSegment(sketch, "E1106", {"start": v(17.66, -12.5) * mm, "end": v(17.66, -12.9) * mm});
            skLineSegment(sketch, "E1107", {"start": v(17.66, -12.9) * mm, "end": v(16.07, -12.9) * mm});
            skLineSegment(sketch, "E1108", {"start": v(16.07, -12.9) * mm, "end": v(16.07, -16.07) * mm});
            skLineSegment(sketch, "E1109", {"start": v(16.07, -16.07) * mm, "end": v(11.31, -16.07) * mm});
            skLineSegment(sketch, "E1110", {"start": v(11.31, -16.07) * mm, "end": v(11.31, -17.26) * mm});
            skLineSegment(sketch, "E1111", {"start": v(11.31, -17.26) * mm, "end": v(18.85, -17.26) * mm});
            skLineSegment(sketch, "E1112", {"start": v(14.09, -9.72) * mm, "end": v(14.09, -6.15) * mm});
            skLineSegment(sketch, "E1113", {"start": v(14.09, -6.15) * mm, "end": v(15.68, -6.15) * mm});
            skLineSegment(sketch, "E1114", {"start": v(15.68, -6.15) * mm, "end": v(15.68, -4.56) * mm});
            skLineSegment(sketch, "E1115", {"start": v(15.68, -4.56) * mm, "end": v(17.26, -4.56) * mm});
            skLineSegment(sketch, "E1116", {"start": v(17.26, -4.56) * mm, "end": v(17.26, -2.98) * mm});
            skLineSegment(sketch, "E1117", {"start": v(17.26, -2.98) * mm, "end": v(19.25, -2.98) * mm});
            skLineSegment(sketch, "E1118", {"start": v(19.25, -2.98) * mm, "end": v(19.25, -9.72) * mm});
            skLineSegment(sketch, "E1119", {"start": v(19.25, -9.72) * mm, "end": v(14.09, -9.72) * mm});
            skLineSegment(sketch, "E1120", {"start": v(18.85, -9.33) * mm, "end": v(18.85, -6.55) * mm});
            skLineSegment(sketch, "E1121", {"start": v(18.85, -6.55) * mm, "end": v(17.26, -6.55) * mm});
            skLineSegment(sketch, "E1122", {"start": v(17.26, -6.55) * mm, "end": v(17.26, -6.15) * mm});
            skLineSegment(sketch, "E1123", {"start": v(17.26, -6.15) * mm, "end": v(18.85, -6.15) * mm});
            skLineSegment(sketch, "E1124", {"start": v(18.85, -6.15) * mm, "end": v(18.85, -3.37) * mm});
            skLineSegment(sketch, "E1125", {"start": v(18.85, -3.37) * mm, "end": v(17.66, -3.37) * mm});
            skLineSegment(sketch, "E1126", {"start": v(17.66, -3.37) * mm, "end": v(17.66, -4.96) * mm});
            skLineSegment(sketch, "E1127", {"start": v(17.66, -4.96) * mm, "end": v(16.07, -4.96) * mm});
            skLineSegment(sketch, "E1128", {"start": v(16.07, -4.96) * mm, "end": v(16.07, -6.55) * mm});
            skLineSegment(sketch, "E1129", {"start": v(16.07, -6.55) * mm, "end": v(14.49, -6.55) * mm});
            skLineSegment(sketch, "E1130", {"start": v(14.49, -6.55) * mm, "end": v(14.49, -7.74) * mm});
            skLineSegment(sketch, "E1131", {"start": v(14.49, -7.74) * mm, "end": v(17.66, -7.74) * mm});
            skLineSegment(sketch, "E1132", {"start": v(17.66, -7.74) * mm, "end": v(17.66, -8.14) * mm});
            skLineSegment(sketch, "E1133", {"start": v(17.66, -8.14) * mm, "end": v(14.49, -8.14) * mm});
            skLineSegment(sketch, "E1134", {"start": v(14.49, -8.14) * mm, "end": v(14.49, -9.33) * mm});
            skLineSegment(sketch, "E1135", {"start": v(14.49, -9.33) * mm, "end": v(18.85, -9.33) * mm});
            skLineSegment(sketch, "E1136", {"start": v(23.61, -16.07) * mm, "end": v(23.61, -15.68) * mm});
            skLineSegment(sketch, "E1137", {"start": v(23.61, -15.68) * mm, "end": v(29.96, -15.68) * mm});
            skLineSegment(sketch, "E1138", {"start": v(29.96, -15.68) * mm, "end": v(29.96, -14.09) * mm});
            skLineSegment(sketch, "E1139", {"start": v(29.96, -14.09) * mm, "end": v(31.55, -14.09) * mm});
            skLineSegment(sketch, "E1140", {"start": v(31.55, -14.09) * mm, "end": v(31.55, -3.37) * mm});
            skLineSegment(sketch, "E1141", {"start": v(31.55, -3.37) * mm, "end": v(29.96, -3.37) * mm});
            skLineSegment(sketch, "E1142", {"start": v(29.96, -3.37) * mm, "end": v(29.96, -1.79) * mm});
            skLineSegment(sketch, "E1143", {"start": v(29.96, -1.79) * mm, "end": v(23.61, -1.79) * mm});
            skLineSegment(sketch, "E1144", {"start": v(23.61, -1.79) * mm, "end": v(23.61, -1.39) * mm});
            skLineSegment(sketch, "E1145", {"start": v(23.61, -1.39) * mm, "end": v(28.38, -1.39) * mm});
            skLineSegment(sketch, "E1146", {"start": v(28.38, -1.39) * mm, "end": v(28.38, -0.2) * mm});
            skLineSegment(sketch, "E1147", {"start": v(28.38, -0.2) * mm, "end": v(22.42, -0.2) * mm});
            skLineSegment(sketch, "E1148", {"start": v(22.42, -0.2) * mm, "end": v(22.42, -2.98) * mm});
            skLineSegment(sketch, "E1149", {"start": v(22.42, -2.98) * mm, "end": v(24.01, -2.98) * mm});
            skLineSegment(sketch, "E1150", {"start": v(24.01, -2.98) * mm, "end": v(24.01, -11.31) * mm});
            skLineSegment(sketch, "E1151", {"start": v(24.01, -11.31) * mm, "end": v(23.61, -11.31) * mm});
            skLineSegment(sketch, "E1152", {"start": v(23.61, -11.31) * mm, "end": v(23.61, -3.37) * mm});
            skLineSegment(sketch, "E1153", {"start": v(23.61, -3.37) * mm, "end": v(22.42, -3.37) * mm});
            skLineSegment(sketch, "E1154", {"start": v(22.42, -3.37) * mm, "end": v(22.42, -8.14) * mm});
            skLineSegment(sketch, "E1155", {"start": v(22.03, -8.14) * mm, "end": v(22.03, 0.2) * mm});
            skLineSegment(sketch, "E1156", {"start": v(22.03, 0.2) * mm, "end": v(33.54, 0.2) * mm});
            skLineSegment(sketch, "E1157", {"start": v(33.54, 0.2) * mm, "end": v(33.54, -8.14) * mm});
            skLineSegment(sketch, "E1158", {"start": v(33.54, -8.14) * mm, "end": v(31.95, -8.14) * mm});
            skLineSegment(sketch, "E1159", {"start": v(31.95, -8.14) * mm, "end": v(31.95, -14.49) * mm});
            skLineSegment(sketch, "E1160", {"start": v(31.95, -14.49) * mm, "end": v(30.36, -14.49) * mm});
            skLineSegment(sketch, "E1161", {"start": v(30.36, -14.49) * mm, "end": v(30.36, -16.07) * mm});
            skLineSegment(sketch, "E1162", {"start": v(30.36, -16.07) * mm, "end": v(23.61, -16.07) * mm});
            skLineSegment(sketch, "E1163", {"start": v(22.03, -17.66) * mm, "end": v(22.03, -9.33) * mm});
            skLineSegment(sketch, "E1164", {"start": v(22.03, -9.33) * mm, "end": v(22.42, -9.33) * mm});
            skLineSegment(sketch, "E1165", {"start": v(22.42, -9.33) * mm, "end": v(22.42, -14.09) * mm});
            skLineSegment(sketch, "E1166", {"start": v(22.42, -14.09) * mm, "end": v(23.61, -14.09) * mm});
            skLineSegment(sketch, "E1167", {"start": v(23.61, -14.09) * mm, "end": v(23.61, -12.5) * mm});
            skLineSegment(sketch, "E1168", {"start": v(23.61, -12.5) * mm, "end": v(24.01, -12.5) * mm});
            skLineSegment(sketch, "E1169", {"start": v(24.01, -12.5) * mm, "end": v(24.01, -14.49) * mm});
            skLineSegment(sketch, "E1170", {"start": v(24.01, -14.49) * mm, "end": v(22.42, -14.49) * mm});
            skLineSegment(sketch, "E1171", {"start": v(22.42, -14.49) * mm, "end": v(22.42, -17.26) * mm});
            skLineSegment(sketch, "E1172", {"start": v(22.42, -17.26) * mm, "end": v(31.55, -17.26) * mm});
            skLineSegment(sketch, "E1173", {"start": v(31.55, -17.26) * mm, "end": v(31.55, -15.68) * mm});
            skLineSegment(sketch, "E1174", {"start": v(31.55, -15.68) * mm, "end": v(31.95, -15.68) * mm});
            skLineSegment(sketch, "E1175", {"start": v(31.95, -15.68) * mm, "end": v(31.95, -17.26) * mm});
            skLineSegment(sketch, "E1176", {"start": v(31.95, -17.26) * mm, "end": v(33.14, -17.26) * mm});
            skLineSegment(sketch, "E1177", {"start": v(33.14, -17.26) * mm, "end": v(33.14, -9.33) * mm});
            skLineSegment(sketch, "E1178", {"start": v(33.14, -9.33) * mm, "end": v(33.54, -9.33) * mm});
            skLineSegment(sketch, "E1179", {"start": v(33.54, -9.33) * mm, "end": v(33.54, -17.66) * mm});
            skLineSegment(sketch, "E1180", {"start": v(33.54, -17.66) * mm, "end": v(22.03, -17.66) * mm});
            skLineSegment(sketch, "E1181", {"start": v(25.2, -14.49) * mm, "end": v(25.2, -6.15) * mm});
            skLineSegment(sketch, "E1182", {"start": v(25.2, -6.15) * mm, "end": v(25.6, -6.15) * mm});
            skLineSegment(sketch, "E1183", {"start": v(25.6, -6.15) * mm, "end": v(25.6, -7.74) * mm});
            skLineSegment(sketch, "E1184", {"start": v(25.6, -7.74) * mm, "end": v(28.77, -7.74) * mm});
            skLineSegment(sketch, "E1185", {"start": v(28.77, -7.74) * mm, "end": v(28.77, -9.72) * mm});
            skLineSegment(sketch, "E1186", {"start": v(28.77, -9.72) * mm, "end": v(28.38, -9.72) * mm});
            skLineSegment(sketch, "E1187", {"start": v(28.38, -9.72) * mm, "end": v(28.38, -8.14) * mm});
            skLineSegment(sketch, "E1188", {"start": v(28.38, -8.14) * mm, "end": v(25.6, -8.14) * mm});
            skLineSegment(sketch, "E1189", {"start": v(25.6, -8.14) * mm, "end": v(25.6, -12.5) * mm});
            skLineSegment(sketch, "E1190", {"start": v(25.6, -12.5) * mm, "end": v(26.79, -12.5) * mm});
            skLineSegment(sketch, "E1191", {"start": v(26.79, -12.5) * mm, "end": v(26.79, -9.33) * mm});
            skLineSegment(sketch, "E1192", {"start": v(26.79, -9.33) * mm, "end": v(27.19, -9.33) * mm});
            skLineSegment(sketch, "E1193", {"start": v(27.19, -9.33) * mm, "end": v(27.19, -10.91) * mm});
            skLineSegment(sketch, "E1194", {"start": v(27.19, -10.91) * mm, "end": v(28.77, -10.91) * mm});
            skLineSegment(sketch, "E1195", {"start": v(28.77, -10.91) * mm, "end": v(28.77, -11.31) * mm});
            skLineSegment(sketch, "E1196", {"start": v(28.77, -11.31) * mm, "end": v(27.19, -11.31) * mm});
            skLineSegment(sketch, "E1197", {"start": v(27.19, -11.31) * mm, "end": v(27.19, -12.9) * mm});
            skLineSegment(sketch, "E1198", {"start": v(27.19, -12.9) * mm, "end": v(25.6, -12.9) * mm});
            skLineSegment(sketch, "E1199", {"start": v(25.6, -12.9) * mm, "end": v(25.6, -14.09) * mm});
            skLineSegment(sketch, "E1200", {"start": v(25.6, -14.09) * mm, "end": v(28.38, -14.09) * mm});
            skLineSegment(sketch, "E1201", {"start": v(28.38, -14.09) * mm, "end": v(28.38, -12.5) * mm});
            skLineSegment(sketch, "E1202", {"start": v(28.38, -12.5) * mm, "end": v(29.96, -12.5) * mm});
            skLineSegment(sketch, "E1203", {"start": v(29.96, -12.5) * mm, "end": v(29.96, -4.96) * mm});
            skLineSegment(sketch, "E1204", {"start": v(29.96, -4.96) * mm, "end": v(28.38, -4.96) * mm});
            skLineSegment(sketch, "E1205", {"start": v(28.38, -4.96) * mm, "end": v(28.38, -3.37) * mm});
            skLineSegment(sketch, "E1206", {"start": v(28.38, -3.37) * mm, "end": v(25.6, -3.37) * mm});
            skLineSegment(sketch, "E1207", {"start": v(25.6, -3.37) * mm, "end": v(25.6, -4.96) * mm});
            skLineSegment(sketch, "E1208", {"start": v(25.6, -4.96) * mm, "end": v(25.2, -4.96) * mm});
            skLineSegment(sketch, "E1209", {"start": v(25.2, -4.96) * mm, "end": v(25.2, -2.98) * mm});
            skLineSegment(sketch, "E1210", {"start": v(25.2, -2.98) * mm, "end": v(28.77, -2.98) * mm});
            skLineSegment(sketch, "E1211", {"start": v(28.77, -2.98) * mm, "end": v(28.77, -4.56) * mm});
            skLineSegment(sketch, "E1212", {"start": v(28.77, -4.56) * mm, "end": v(30.36, -4.56) * mm});
            skLineSegment(sketch, "E1213", {"start": v(30.36, -4.56) * mm, "end": v(30.36, -12.9) * mm});
            skLineSegment(sketch, "E1214", {"start": v(30.36, -12.9) * mm, "end": v(28.77, -12.9) * mm});
            skLineSegment(sketch, "E1215", {"start": v(28.77, -12.9) * mm, "end": v(28.77, -14.49) * mm});
            skLineSegment(sketch, "E1216", {"start": v(28.77, -14.49) * mm, "end": v(25.2, -14.49) * mm});
            skLineSegment(sketch, "E1217", {"start": v(26.79, -6.55) * mm, "end": v(26.79, -4.56) * mm});
            skLineSegment(sketch, "E1218", {"start": v(26.79, -4.56) * mm, "end": v(27.19, -4.56) * mm});
            skLineSegment(sketch, "E1219", {"start": v(27.19, -4.56) * mm, "end": v(27.19, -6.15) * mm});
            skLineSegment(sketch, "E1220", {"start": v(27.19, -6.15) * mm, "end": v(28.77, -6.15) * mm});
            skLineSegment(sketch, "E1221", {"start": v(28.77, -6.15) * mm, "end": v(28.77, -6.55) * mm});
            skLineSegment(sketch, "E1222", {"start": v(28.77, -6.55) * mm, "end": v(26.79, -6.55) * mm});
            skLineSegment(sketch, "E1223", {"start": v(33.14, -7.74) * mm, "end": v(33.14, -1.79) * mm});
            skLineSegment(sketch, "E1224", {"start": v(33.14, -1.79) * mm, "end": v(31.55, -1.79) * mm});
            skLineSegment(sketch, "E1225", {"start": v(31.55, -1.79) * mm, "end": v(31.55, -1.39) * mm});
            skLineSegment(sketch, "E1226", {"start": v(31.55, -1.39) * mm, "end": v(33.14, -1.39) * mm});
            skLineSegment(sketch, "E1227", {"start": v(33.14, -1.39) * mm, "end": v(33.14, -0.2) * mm});
            skLineSegment(sketch, "E1228", {"start": v(33.14, -0.2) * mm, "end": v(28.77, -0.2) * mm});
            skLineSegment(sketch, "E1229", {"start": v(28.77, -0.2) * mm, "end": v(28.77, -1.39) * mm});
            skLineSegment(sketch, "E1230", {"start": v(28.77, -1.39) * mm, "end": v(30.36, -1.39) * mm});
            skLineSegment(sketch, "E1231", {"start": v(30.36, -1.39) * mm, "end": v(30.36, -2.98) * mm});
            skLineSegment(sketch, "E1232", {"start": v(30.36, -2.98) * mm, "end": v(31.95, -2.98) * mm});
            skLineSegment(sketch, "E1233", {"start": v(31.95, -2.98) * mm, "end": v(31.95, -7.74) * mm});
            skLineSegment(sketch, "E1234", {"start": v(31.95, -7.74) * mm, "end": v(33.14, -7.74) * mm});
            skLineSegment(sketch, "E1235", {"start": v(9.67, -0.2) * mm, "end": v(8.14, -0.2) * mm});
            skLineSegment(sketch, "E1236", {"start": v(9.68, -0.2) * mm, "end": v(9.67, -0.2) * mm});
            skLineSegment(sketch, "E1237", {"start": v(9.67, 0.2) * mm, "end": v(9.68, -0.2) * mm});
            skLineSegment(sketch, "E1238.trimOffspring", {"start": v(9.68, -0.2) * mm, "end": v(-0.2, -0.2) * mm});
            skLineSegment(sketch, "E1239", {"start": v(7.74, -1.39) * mm, "end": v(8.14, -1.39) * mm});
            skLineSegment(sketch, "E1240", {"start": v(-11.31, 17.26) * mm, "end": v(-10.91, 17.26) * mm});
            skLineSegment(sketch, "E1241", {"start": v(-11.31, 16.07) * mm, "end": v(-10.91, 16.07) * mm});
            skLineSegment(sketch, "E1242", {"start": v(-3.37, 16.07) * mm, "end": v(-2.98, 16.07) * mm});
            skLineSegment(sketch, "E1243", {"start": v(-3.37, 17.26) * mm, "end": v(-2.98, 17.26) * mm});
            skSolve(sketch);
        }
        {
            var Q0;
            Q0 = qSketchRegion(id + "F0", true);
            extrude(context, id + "F1", {"entities" : qUnion([Q0]), "depth" : 25 * mm, "offsetDistance" : 25 * mm});
        }
        {
            var Q0;
            Q0=makeQuery(id+"F1.opExtrude","SWEPT_EDGE",EDGE,{"disambiguationData":[OSD([sQuery(id+"F0.wireOp",EDGE,"E1179"),sQuery(id+"F0.wireOp",EDGE,"E1180")])]});
            var Q1;
            Q1=makeQuery(id+"F1.opExtrude","SWEPT_EDGE",EDGE,{"disambiguationData":[OSD([sQuery(id+"F0.wireOp",EDGE,"E537"),sQuery(id+"F0.wireOp",EDGE,"E538")])]});
            var Q2;
            Q2=makeQuery(id+"F1.opExtrude","SWEPT_EDGE",EDGE,{"disambiguationData":[OSD([sQuery(id+"F0.wireOp",EDGE,"E38"),sQuery(id+"F0.wireOp",EDGE,"E39")])]});
            var Q3;
            Q3=makeQuery(id+"F1.opExtrude","SWEPT_EDGE",EDGE,{"disambiguationData":[OSD([sQuery(id+"F0.wireOp",EDGE,"E661"),sQuery(id+"F0.wireOp",EDGE,"E734")])]});
            var Q4;
            Q4=makeQuery(id+"F1.opExtrude","CAP_EDGE",EDGE,{"disambiguationData":[OSD([sQuery(id+"F0.wireOp",EDGE,"E39"),sQuery(id+"F0.wireOp",EDGE,"E121"),sQuery(id+"F0.wireOp",EDGE,"E238"),sQuery(id+"F0.wireOp",EDGE,"E312"),sQuery(id+"F0.wireOp",EDGE,"E444"),sQuery(id+"F0.wireOp",EDGE,"E537")])],"isStart":false});
            var Q5;
            Q5=makeQuery(id+"F1.opExtrude","CAP_EDGE",EDGE,{"disambiguationData":[OSD([sQuery(id+"F0.wireOp",EDGE,"E38")])],"isStart":false});
            var Q6;
            Q6=makeQuery(id+"F1.opExtrude","CAP_EDGE",EDGE,{"disambiguationData":[OSD([sQuery(id+"F0.wireOp",EDGE,"E46"),sQuery(id+"F0.wireOp",EDGE,"E653")])],"isStart":false});
            var Q7;
            Q7=makeQuery(id+"F1.opExtrude","CAP_EDGE",EDGE,{"disambiguationData":[OSD([sQuery(id+"F0.wireOp",EDGE,"E661")])],"isStart":false});
            var Q8;
            Q8=makeQuery(id+"F1.opExtrude","CAP_EDGE",EDGE,{"disambiguationData":[OSD([sQuery(id+"F0.wireOp",EDGE,"E734"),sQuery(id+"F0.wireOp",EDGE,"E791"),sQuery(id+"F0.wireOp",EDGE,"E895"),sQuery(id+"F0.wireOp",EDGE,"E1031"),sQuery(id+"F0.wireOp",EDGE,"E1095"),sQuery(id+"F0.wireOp",EDGE,"E1180")])],"isStart":false});
            var Q9;
            Q9=makeQuery(id+"F1.opExtrude","CAP_EDGE",EDGE,{"disambiguationData":[OSD([sQuery(id+"F0.wireOp",EDGE,"E1179")])],"isStart":false});
            var Q10;
            Q10=makeQuery(id+"F1.opExtrude","CAP_EDGE",EDGE,{"disambiguationData":[OSD([sQuery(id+"F0.wireOp",EDGE,"E559"),sQuery(id+"F0.wireOp",EDGE,"E1157")])],"isStart":false});
            var Q11;
            Q11=makeQuery(id+"F1.opExtrude","CAP_EDGE",EDGE,{"disambiguationData":[OSD([sQuery(id+"F0.wireOp",EDGE,"E538")])],"isStart":false});
            fillet(context, id + "F2", {"entities" : qUnion([Q0, Q1, Q2, Q3, Q4, Q5, Q6, Q7, Q8, Q9, Q10, Q11]), "radius" : 5 * mm, "tangentPropagation" : true, "allowEdgeOverflow" : false});
        }
    });
